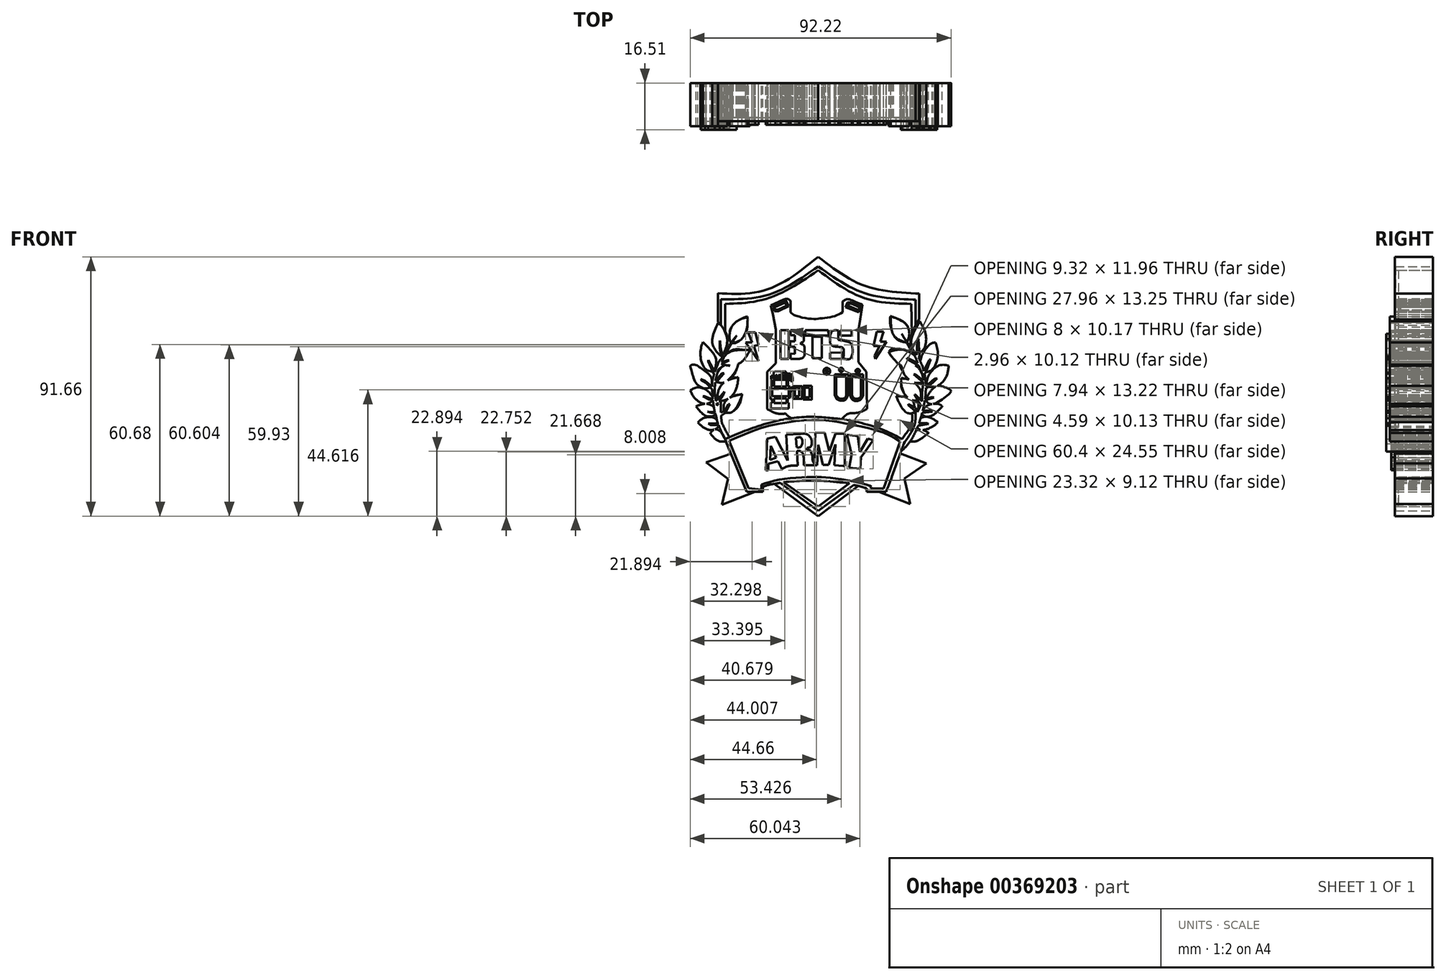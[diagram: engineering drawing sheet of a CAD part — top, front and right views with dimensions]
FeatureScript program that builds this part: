
annotation { "Feature Type Name" : "Feature", "Feature Type Description" : "" }
export const myFeature = defineFeature(function(context is Context, id is Id, definition is map)
    precondition{}
    {
        {
            var Q0;
            Q0=qCreatedBy(makeId("Front.planeOp"),FACE);
            var sketch = newSketch(context, id + "F0", { "sketchPlane" : qUnion([Q0])});
            skFitSpline(sketch, "E0", {"points": [v(-30.19, 8) * mm, v(-27.2, 9.29) * mm, v(-25.23, 13.15) * mm, v(-24.96, 17.16) * mm], "startDerivative": vector(10.5, 2.6) * mm, "endDerivative": vector(-0.16, 11.52) * mm});
            skFitSpline(sketch, "E1", {"points": [v(-24.96, 17.16) * mm, v(-28.56, 15.8) * mm, v(-31.07, 12.48) * mm, v(-31, 8.26) * mm, v(-30.19, 8) * mm], "startDerivative": vector(-13.43, -3.63) * mm, "endDerivative": vector(6.8, 0.18) * mm});
            skFitSpline(sketch, "E2", {"points": [v(-34.2, 3.24) * mm, v(-36.37, 5.48) * mm, v(-37.45, 9.08) * mm, v(-35.42, 15.06) * mm], "startDerivative": vector(-8.23, 7.14) * mm, "endDerivative": vector(7.27, 15.47) * mm});
            skFitSpline(sketch, "E3", {"points": [v(-34.2, 3.24) * mm, v(-32.9, 5.55) * mm, v(-32.23, 9.56) * mm, v(-34.2, 14.04) * mm, v(-35.42, 15.06) * mm], "startDerivative": vector(5.9, 9.32) * mm, "endDerivative": vector(-6.57, 4.06) * mm});
            skFitSpline(sketch, "E4", {"points": [v(-36.9, -2.26) * mm, v(-36.1, 0.6) * mm, v(-36.43, 3.24) * mm, v(-40.78, 8.26) * mm], "startDerivative": vector(3.44, 9.98) * mm, "endDerivative": vector(-12.5, 12.2) * mm});
            skFitSpline(sketch, "E5", {"points": [v(-36.9, -2.26) * mm, v(-39.56, -1.44) * mm, v(-41.4, 1.82) * mm, v(-41.46, 6.1) * mm, v(-40.78, 8.26) * mm], "startDerivative": vector(-12.2, 1.64) * mm, "endDerivative": vector(3.69, 9.25) * mm});
            skFitSpline(sketch, "E6", {"points": [v(-34.26, 0.6) * mm, v(-31.27, 0) * mm, v(-27.2, 1.2) * mm, v(-24.15, 5.48) * mm], "startDerivative": vector(9.82, -3) * mm, "endDerivative": vector(6.9, 13.15) * mm});
            skFitSpline(sketch, "E7", {"points": [v(-34.26, 0.6) * mm, v(-32.43, 4.06) * mm, v(-28.5, 5.48) * mm, v(-24.15, 5.48) * mm], "startDerivative": vector(4.12, 12.1) * mm, "endDerivative": vector(12.58, -0.7) * mm});
            skFitSpline(sketch, "E8", {"points": [v(-37.66, -7.35) * mm, v(-37.86, -4.09) * mm, v(-40.78, -1.44) * mm, v(-43.5, 0.3) * mm, v(-45.26, 0) * mm], "startDerivative": vector(1.6, 13.32) * mm, "endDerivative": vector(-8.96, -3.42) * mm});
            skFitSpline(sketch, "E9", {"points": [v(-37.66, -7.35) * mm, v(-39.56, -8.1) * mm, v(-42.82, -6.6) * mm, v(-44.68, -2.26) * mm, v(-45.26, 0) * mm], "startDerivative": vector(-8.4, -5.24) * mm, "endDerivative": vector(-2.34, 9.18) * mm});
            skFitSpline(sketch, "E10", {"points": [v(-36.4, -5.58) * mm, v(-33.33, -6) * mm, v(-29.37, -2.26) * mm, v(-28.26, 0.6) * mm], "startDerivative": vector(9.84, -3.85) * mm, "endDerivative": vector(2.3, 8.84) * mm});
            skFitSpline(sketch, "E11", {"points": [v(-36.4, -5.58) * mm, v(-35.4, -2.26) * mm, v(-33.33, 0.3) * mm], "startDerivative": vector(1.38, 6.92) * mm, "endDerivative": vector(4.77, 4.85) * mm});
            skFitSpline(sketch, "E12", {"points": [v(-35.4, -12.71) * mm, v(-35.4, -9.32) * mm, v(-33.27, -5.97) * mm, v(-28.26, -4.09) * mm], "startDerivative": vector(-1.3, 11.27) * mm, "endDerivative": vector(14.74, 3.55) * mm});
            skFitSpline(sketch, "E13", {"points": [v(-35.4, -12.71) * mm, v(-31.2, -11.35) * mm, v(-28.83, -7.7) * mm, v(-28.26, -4.09) * mm], "startDerivative": vector(13.25, 2.2) * mm, "endDerivative": vector(0.85, 11.32) * mm});
            skFitSpline(sketch, "E14", {"points": [v(-36.9, -12.03) * mm, v(-39.56, -13.53) * mm, v(-43.22, -11.96) * mm, v(-45.26, -8.77) * mm], "startDerivative": vector(-7.9, -6.9) * mm, "endDerivative": vector(-4.64, 9.96) * mm});
            skFitSpline(sketch, "E15", {"points": [v(-36.9, -12.03) * mm, v(-38.97, -9.05) * mm, v(-42.61, -7.7) * mm, v(-45.26, -8.77) * mm], "startDerivative": vector(-4.78, 9.51) * mm, "endDerivative": vector(-8.06, -5.02) * mm});
            skFitSpline(sketch, "E16", {"points": [v(-33.28, -16.41) * mm, v(-30.23, -16.27) * mm, v(-27.25, -11.35) * mm, v(-26.88, -10.09) * mm], "startDerivative": vector(9.47, -2.39) * mm, "endDerivative": vector(0.94, 4.4) * mm});
            skFitSpline(sketch, "E17", {"points": [v(-33.28, -16.41) * mm, v(-33.28, -13.5) * mm, v(-31.2, -11.35) * mm, v(-26.88, -10.09) * mm], "startDerivative": vector(-1.48, 9.93) * mm, "endDerivative": vector(12.19, 2.44) * mm});
            skFitSpline(sketch, "E18", {"points": [v(-35.38, -16.41) * mm, v(-36.91, -17.72) * mm, v(-39.82, -17.72) * mm, v(-43.23, -14.38) * mm], "startDerivative": vector(-4.87, -5.65) * mm, "endDerivative": vector(-7.8, 10.14) * mm});
            skFitSpline(sketch, "E19", {"points": [v(-35.38, -16.41) * mm, v(-37.06, -14.52) * mm, v(-39.56, -13.53) * mm, v(-43.23, -14.38) * mm], "startDerivative": vector(-4.92, 6.62) * mm, "endDerivative": vector(-10.15, -3.6) * mm});
            skFitSpline(sketch, "E20", {"points": [v(-34.66, -20.92) * mm, v(-36.47, -22.51) * mm, v(-39.56, -22.44) * mm, v(-42.5, -20.12) * mm], "startDerivative": vector(-5.28, -6.44) * mm, "endDerivative": vector(-7.41, 7.58) * mm});
            skFitSpline(sketch, "E21", {"points": [v(-34.66, -20.92) * mm, v(-36.62, -18.6) * mm, v(-40.18, -18.45) * mm, v(-42.5, -20.12) * mm], "startDerivative": vector(-4.76, 8.44) * mm, "endDerivative": vector(-6.36, -6.26) * mm});
            skFitSpline(sketch, "E22", {"points": [v(-32.55, -26.73) * mm, v(-35.18, -26.73) * mm, v(-38.22, -23.9) * mm], "startDerivative": vector(-6.04, -1.13) * mm, "endDerivative": vector(-5.32, 6.5) * mm});
            skFitSpline(sketch, "E23", {"points": [v(-32.55, -26.73) * mm, v(-34.08, -23.97) * mm, v(-34.66, -23.1) * mm], "startDerivative": vector(-2.66, 4.98) * mm, "endDerivative": vector(-1.44, 2.03) * mm});
            skFitSpline(sketch, "E24", {"points": [v(-34.48, -23.34) * mm, v(-36.47, -22.51) * mm, v(-38.16, -23.97) * mm], "startDerivative": vector(-4.18, 2.8) * mm, "endDerivative": vector(-3.17, -4.03) * mm});
            skFitSpline(sketch, "E25", {"points": [v(31.17, 8.2) * mm, v(28.13, 9.37) * mm, v(26.18, 11.82) * mm, v(25.69, 17.4) * mm], "startDerivative": vector(-10.62, 3.25) * mm, "endDerivative": vector(0.13, 15.42) * mm});
            skFitSpline(sketch, "E26", {"points": [v(31.17, 8.2) * mm, v(32.15, 10.35) * mm, v(31.17, 14.46) * mm, v(25.69, 17.4) * mm], "startDerivative": vector(4.76, 7.94) * mm, "endDerivative": vector(-15.88, 5.4) * mm});
            skFitSpline(sketch, "E27", {"points": [v(34.79, 3.6) * mm, v(37.62, 6.44) * mm, v(37.92, 11.33) * mm, v(35.96, 15.63) * mm], "startDerivative": vector(10.72, 7.67) * mm, "endDerivative": vector(-6.93, 11.9) * mm});
            skFitSpline(sketch, "E28", {"points": [v(34.79, 3.6) * mm, v(32.83, 8.2) * mm, v(35.96, 15.63) * mm], "startDerivative": vector(-6.65, 9.81) * mm, "endDerivative": vector(8.4, 14.08) * mm});
            skFitSpline(sketch, "E29", {"points": [v(34.79, 0) * mm, v(32.15, 0) * mm, v(29.4, 0) * mm, v(25.69, 3.6) * mm, v(24.7, 5.36) * mm], "startDerivative": vector(-11.4, 0.72) * mm, "endDerivative": vector(-3.42, 7.43) * mm});
            skFitSpline(sketch, "E30", {"points": [v(34.79, 0) * mm, v(34.79, 2.62) * mm, v(31.17, 5.26) * mm, v(28.23, 5.66) * mm, v(24.94, 4.86) * mm], "startDerivative": vector(2.96, 12.02) * mm, "endDerivative": vector(-13.45, -4.04) * mm});
            skFitSpline(sketch, "E31", {"points": [v(37.43, -2.46) * mm, v(40.27, -1.39) * mm, v(42.32, 3.6) * mm, v(41.44, 8.2) * mm], "startDerivative": vector(10.74, 1.63) * mm, "endDerivative": vector(-4.28, 12.5) * mm});
            skFitSpline(sketch, "E32", {"points": [v(37.43, -2.46) * mm, v(35.96, 0.96) * mm, v(39.29, 7.32) * mm, v(41.44, 8.2) * mm], "startDerivative": vector(-7.42, 9.22) * mm, "endDerivative": vector(8.15, 1.13) * mm});
            skFitSpline(sketch, "E33", {"points": [v(38.3, -7.45) * mm, v(41.44, -7.45) * mm, v(45.06, -4.32) * mm, v(46.14, 0) * mm], "startDerivative": vector(10.39, 0.61) * mm, "endDerivative": vector(1.3, 12.96) * mm});
            skFitSpline(sketch, "E34", {"points": [v(38.3, -7.45) * mm, v(39, -3.64) * mm, v(42.61, 0) * mm, v(46.14, 0) * mm], "startDerivative": vector(0.09, 13.1) * mm, "endDerivative": vector(11.66, -2.26) * mm});
            skFitSpline(sketch, "E35", {"points": [v(38.3, -12.25) * mm, v(40.27, -13.62) * mm, v(45.25, -10.88) * mm, v(46.93, -8.82) * mm, v(44.18, -7.45) * mm, v(41.44, -7.45) * mm, v(38.3, -12.25) * mm]});
            skFitSpline(sketch, "E36", {"points": [v(36.16, -16.65) * mm, v(37.92, -18.02) * mm, v(40.36, -17.63) * mm, v(43.89, -14.4) * mm], "startDerivative": vector(5.7, -6.05) * mm, "endDerivative": vector(8.4, 9.26) * mm});
            skFitSpline(sketch, "E37", {"points": [v(36.16, -16.65) * mm, v(38.3, -14.3) * mm, v(40.27, -13.62) * mm, v(42.61, -13.62) * mm, v(43.89, -14.4) * mm], "startDerivative": vector(7.08, 9.2) * mm, "endDerivative": vector(5.46, -4.64) * mm});
            skFitSpline(sketch, "E38", {"points": [v(36.16, -12.25) * mm, v(33.32, -12.25) * mm, v(30.48, -10) * mm, v(29.3, -6.08) * mm, v(29.3, -4.52) * mm], "startDerivative": vector(-11.56, -1.6) * mm, "endDerivative": vector(0.5, 7.43) * mm});
            skFitSpline(sketch, "E39", {"points": [v(36.16, -12.25) * mm, v(36.16, -8.92) * mm, v(33.12, -5.4) * mm, v(29.3, -4.52) * mm], "startDerivative": vector(1.87, 10.7) * mm, "endDerivative": vector(-11.7, 0.9) * mm});
            skFitSpline(sketch, "E40", {"points": [v(34, -16.65) * mm, v(31.26, -16.65) * mm, v(28.13, -12.25) * mm, v(27.45, -10.2) * mm], "startDerivative": vector(-9.07, -2.55) * mm, "endDerivative": vector(-1.62, 6.4) * mm});
            skFitSpline(sketch, "E41", {"points": [v(34, -16.65) * mm, v(34, -14.4) * mm, v(33.32, -12.25) * mm, v(31.56, -11.28) * mm, v(27.6, -10.77) * mm], "startDerivative": vector(0.5, 9.44) * mm, "endDerivative": vector(-13.88, 1.15) * mm});
            skFitSpline(sketch, "E42", {"points": [v(34.66, -21.04) * mm, v(36.17, -22.78) * mm, v(40.46, -21.54) * mm, v(42.28, -20.04) * mm], "startDerivative": vector(3.62, -7.81) * mm, "endDerivative": vector(4.77, 4.93) * mm});
            skFitSpline(sketch, "E43", {"points": [v(34.66, -21.04) * mm, v(35.62, -19.03) * mm, v(38.5, -18.13) * mm, v(42.28, -20.04) * mm], "startDerivative": vector(2.13, 7.76) * mm, "endDerivative": vector(9.59, -6.77) * mm});
            skFitSpline(sketch, "E44", {"points": [v(32.29, -26.75) * mm, v(33.66, -24.74) * mm, v(34.66, -22.82) * mm], "startDerivative": vector(2.81, 3.9) * mm, "endDerivative": vector(1.92, 3.96) * mm});
            skFitSpline(sketch, "E45", {"points": [v(32.29, -26.75) * mm, v(34.66, -26.75) * mm, v(39.04, -23.78) * mm], "startDerivative": vector(5.64, -1) * mm, "endDerivative": vector(7.73, 6.44) * mm});
            skFitSpline(sketch, "E46", {"points": [v(34.66, -22.82) * mm, v(37, -22.82) * mm, v(39.04, -23.78) * mm], "startDerivative": vector(4.77, 0.49) * mm, "endDerivative": vector(4, -2.41) * mm});
            skFitSpline(sketch, "E47", {"points": [v(-33.33, 0.3) * mm, v(-31.27, 0) * mm, v(-28.26, 0.6) * mm], "startDerivative": vector(4.34, -1.08) * mm, "endDerivative": vector(5.76, 1.57) * mm});
            skFitSpline(sketch, "E48", {"points": [v(36.92, -6.05) * mm, v(34.07, -6.05) * mm, v(30.8, -3.64) * mm, v(29.4, 0) * mm], "startDerivative": vector(-9.37, -1.43) * mm, "endDerivative": vector(-2.65, 10.96) * mm});
            skFitSpline(sketch, "E49", {"points": [v(36.92, -6.05) * mm, v(36.92, -3.64) * mm, v(34.34, 0.03) * mm, v(29.4, 0) * mm], "startDerivative": vector(1.31, 8.33) * mm, "endDerivative": vector(-14.13, -2.96) * mm});
            skSolve(sketch);
        }
        {
            var Q0;
            Q0=qCreatedBy(makeId("Front.planeOp"),FACE);
            var sketch = newSketch(context, id + "F1", { "sketchPlane" : qUnion([Q0])});
            skFitSpline(sketch, "E50", {"points": [v(-35.48, 25.53) * mm, v(-17.96, 26.92) * mm, v(0, 38.42) * mm], "startDerivative": vector(37.43, -1.62) * mm, "endDerivative": vector(33.59, 26.94) * mm});
            skFitSpline(sketch, "E51", {"points": [v(0, 38.42) * mm, v(16.05, 28.37) * mm, v(34.4, 25.5) * mm], "startDerivative": vector(30.7, -23.57) * mm, "endDerivative": vector(38.12, -2.26) * mm});
            skLineSegment(sketch, "E52", {"start": v(-35.48, 25.53) * mm, "end": v(-35.48, 15.4) * mm});
            skLineSegment(sketch, "E53", {"start": v(-35.48, 15.4) * mm, "end": v(-34.38, 14.35) * mm});
            skLineSegment(sketch, "E54", {"start": v(-34.38, 14.35) * mm, "end": v(-34.38, 23.46) * mm});
            skFitSpline(sketch, "E55", {"points": [v(-34.38, 23.46) * mm, v(-17.39, 25.15) * mm, v(0, 35.04) * mm], "startDerivative": vector(35.88, -0.2) * mm, "endDerivative": vector(32.95, 23.07) * mm});
            skFitSpline(sketch, "E56", {"points": [v(0, 35.04) * mm, v(16.05, 25.74) * mm, v(33.52, 23.3) * mm], "startDerivative": vector(30.76, -21.78) * mm, "endDerivative": vector(36.3, -1.62) * mm});
            skLineSegment(sketch, "E57", {"start": v(34.4, 25.5) * mm, "end": v(35.72, 25.5) * mm});
            skLineSegment(sketch, "E58", {"start": v(35.72, 25.5) * mm, "end": v(35.72, 16.36) * mm});
            skLineSegment(sketch, "E59", {"start": v(35.72, 16.36) * mm, "end": v(34.4, 14.33) * mm});
            skLineSegment(sketch, "E60", {"start": v(34.4, 14.33) * mm, "end": v(34.4, 23.3) * mm});
            skLineSegment(sketch, "E61", {"start": v(34.4, 23.3) * mm, "end": v(33.52, 23.3) * mm});
            skLineSegment(sketch, "E62", {"start": v(-34.38, 14.35) * mm, "end": v(-34.38, 14.33) * mm});
            skLineSegment(sketch, "E63", {"start": v(-32.88, 21.84) * mm, "end": v(-32.88, 12.15) * mm});
            skLineSegment(sketch, "E64", {"start": v(-32.88, 12.15) * mm, "end": v(-34.38, 14.33) * mm});
            skLineSegment(sketch, "E65", {"start": v(34.4, 14.33) * mm, "end": v(33.13, 10.98) * mm});
            skFitSpline(sketch, "E66", {"points": [v(-32.88, 21.84) * mm, v(-17.25, 23.97) * mm, v(0, 33.72) * mm], "startDerivative": vector(33.29, 0.5) * mm, "endDerivative": vector(32.48, 22.28) * mm});
            skFitSpline(sketch, "E67", {"points": [v(0, 33.72) * mm, v(16.05, 23.97) * mm, v(32.92, 21.84) * mm], "startDerivative": vector(30.35, -22.74) * mm, "endDerivative": vector(34.37, -0.2) * mm});
            skLineSegment(sketch, "E68", {"start": v(32.92, 21.84) * mm, "end": v(33.13, 10.98) * mm});
            skLineSegment(sketch, "E69", {"start": v(-35.48, 25.53) * mm, "end": v(-32.84, 26.82) * mm});
            skFitSpline(sketch, "E70", {"points": [v(-32.84, 26.82) * mm, v(-17.96, 28.82) * mm, v(0, 38.42) * mm], "startDerivative": vector(31.94, 1.22) * mm, "endDerivative": vector(33.7, 21.47) * mm});
            skLineSegment(sketch, "E71", {"start": v(35.72, 25.5) * mm, "end": v(32.96, 27.12) * mm});
            skFitSpline(sketch, "E72", {"points": [v(32.96, 27.12) * mm, v(16.05, 29.83) * mm, v(0, 38.42) * mm], "startDerivative": vector(-35.02, 2.69) * mm, "endDerivative": vector(-30.92, 19.82) * mm});
            skFitSpline(sketch, "E73", {"points": [v(-32.88, 12.15) * mm, v(-32.05, 9.37) * mm, v(-32.88, 4.8) * mm], "startDerivative": vector(2.6, -5.84) * mm, "endDerivative": vector(-2.42, -8.3) * mm});
            skFitSpline(sketch, "E74", {"points": [v(-35.48, 15.4) * mm, v(-36.95, 12.15) * mm, v(-37.32, 8.02) * mm, v(-35.97, 4.59) * mm, v(-34.09, 2.66) * mm], "startDerivative": vector(-6.38, -11.95) * mm, "endDerivative": vector(6.56, -7.11) * mm});
            skFitSpline(sketch, "E75", {"points": [v(-34.75, 8.82) * mm, v(-34.75, 5.87) * mm, v(-33.86, 3.18) * mm], "startDerivative": vector(-0.51, -5.9) * mm, "endDerivative": vector(2.47, -4.8) * mm});
            skFitSpline(sketch, "E76", {"points": [v(-33.44, 3.88) * mm, v(-33.95, 4.57) * mm, v(-34.39, 5.87) * mm, v(-34.75, 8.82) * mm], "startDerivative": vector(-1.94, 2.54) * mm, "endDerivative": vector(-0.63, 7.04) * mm});
            skFitSpline(sketch, "E77", {"points": [v(-30.85, 8) * mm, v(-31.29, 11.2) * mm, v(-30.57, 13.69) * mm, v(-26.06, 17.04) * mm, v(-24.97, 17.3) * mm], "startDerivative": vector(-1.4, 12.48) * mm, "endDerivative": vector(5.47, 0.32) * mm});
            skFitSpline(sketch, "E78", {"points": [v(-30.53, 8) * mm, v(-29.15, 8) * mm, v(-26.31, 10.31) * mm, v(-25.13, 13.15) * mm, v(-24.97, 17.3) * mm], "startDerivative": vector(8.6, -1.68) * mm, "endDerivative": vector(-0.22, 15.04) * mm});
            skFitSpline(sketch, "E79", {"points": [v(-34.32, 0.69) * mm, v(-31.47, -0.37) * mm, v(-26.55, 1.82) * mm, v(-24.4, 5.17) * mm], "startDerivative": vector(8.72, -5.5) * mm, "endDerivative": vector(4.72, 10.6) * mm});
            skFitSpline(sketch, "E80", {"points": [v(-32.61, 3.95) * mm, v(-29.8, 5.64) * mm, v(-24.4, 5.17) * mm], "startDerivative": vector(5.74, 4.88) * mm, "endDerivative": vector(10.48, -2.16) * mm});
            skFitSpline(sketch, "E81", {"points": [v(-36.38, -5.86) * mm, v(-33.3, -6.06) * mm, v(-29.76, -3.25) * mm, v(-28.31, 0.59) * mm], "startDerivative": vector(9.85, -3.58) * mm, "endDerivative": vector(2.78, 11.3) * mm});
            skFitSpline(sketch, "E82", {"points": [v(-35.26, -1.35) * mm, v(-34.17, -0.51) * mm, v(-33.1, 0) * mm], "startDerivative": vector(1.95, 1.82) * mm, "endDerivative": vector(2.24, 0.92) * mm});
            skFitSpline(sketch, "E83", {"points": [v(-37.2, -2.17) * mm, v(-39.89, -1.24) * mm, v(-41.43, 2) * mm, v(-41.23, 7.88) * mm, v(-40.92, 8.55) * mm], "startDerivative": vector(-11.92, 2.33) * mm, "endDerivative": vector(2.54, 3.57) * mm});
            skFitSpline(sketch, "E84", {"points": [v(-35.96, -0.73) * mm, v(-36.02, 3.03) * mm, v(-40.92, 8.55) * mm], "startDerivative": vector(1.42, 9) * mm, "endDerivative": vector(-10.77, 9.58) * mm});
            skFitSpline(sketch, "E85", {"points": [v(-38.28, -7.54) * mm, v(-40.92, -7.63) * mm, v(-44.73, -3.25) * mm, v(-45.6, 0) * mm], "startDerivative": vector(-8.99, -2.33) * mm, "endDerivative": vector(-0.88, 9.59) * mm});
            skFitSpline(sketch, "E86", {"points": [v(-37.93, -7.01) * mm, v(-38.24, -3.92) * mm, v(-41.43, -0.73) * mm, v(-45.6, 0) * mm], "startDerivative": vector(0.72, 10.17) * mm, "endDerivative": vector(-11.2, 0.59) * mm});
            skFitSpline(sketch, "E87", {"points": [v(-35.04, -12.58) * mm, v(-32.36, -12.37) * mm, v(-29.69, -9.38) * mm, v(-28.76, -5.86) * mm, v(-28.8, -4.28) * mm], "startDerivative": vector(11.3, -1.17) * mm, "endDerivative": vector(-0.76, 7.7) * mm});
            skFitSpline(sketch, "E88", {"points": [v(-28.8, -4.28) * mm, v(-30.05, -4.28) * mm, v(-31.09, -4.76) * mm], "startDerivative": vector(-2.49, 0.26) * mm, "endDerivative": vector(-1.87, -1.22) * mm});
            skFitSpline(sketch, "E89", {"points": [v(-32.73, -16.65) * mm, v(-30.2, -16.18) * mm, v(-27.83, -13.6) * mm, v(-27.1, -10.41) * mm], "startDerivative": vector(8.44, 0.24) * mm, "endDerivative": vector(1.01, 9.46) * mm});
            skFitSpline(sketch, "E90", {"points": [v(-33.42, -16.24) * mm, v(-33.24, -13.71) * mm, v(-32.36, -12.37) * mm], "startDerivative": vector(-0.06, 3.41) * mm, "endDerivative": vector(2.13, 2.56) * mm});
            skFitSpline(sketch, "E91", {"points": [v(-30.68, -10.97) * mm, v(-28.8, -10.41) * mm, v(-27.1, -10.41) * mm], "startDerivative": vector(3.65, 1.34) * mm, "endDerivative": vector(3.5, -0.26) * mm});
            skFitSpline(sketch, "E92", {"points": [v(-37.19, -12.58) * mm, v(-39.8, -13.5) * mm, v(-43.08, -12.37) * mm, v(-45.92, -8.83) * mm], "startDerivative": vector(-8.47, -4.4) * mm, "endDerivative": vector(-6.77, 10.62) * mm});
            skFitSpline(sketch, "E93", {"points": [v(-37.37, -10.41) * mm, v(-39.87, -8.54) * mm, v(-42.79, -7.75) * mm, v(-45.92, -8.83) * mm], "startDerivative": vector(-7.16, 6.25) * mm, "endDerivative": vector(-9.16, -4.01) * mm});
            skFitSpline(sketch, "E94", {"points": [v(-36.11, -17.76) * mm, v(-38.49, -18.33) * mm, v(-42.28, -16.04) * mm, v(-43.08, -14.66) * mm], "startDerivative": vector(-6.75, -3.48) * mm, "endDerivative": vector(-1.86, 4.98) * mm});
            skFitSpline(sketch, "E95", {"points": [v(-40.84, -13.41) * mm, v(-43.08, -14.66) * mm], "startDerivative": vector(-2.24, -1.23) * mm, "endDerivative": vector(-2.24, -1.23) * mm});
            skFitSpline(sketch, "E96", {"points": [v(-36.94, -14.42) * mm, v(-38.05, -13.86) * mm, v(-39.8, -13.5) * mm], "startDerivative": vector(-2.27, 1.36) * mm, "endDerivative": vector(-3.42, 0.52) * mm});
            skFitSpline(sketch, "E97", {"points": [v(-35, -21.58) * mm, v(-36.37, -22.66) * mm, v(-38.95, -22.6) * mm, v(-42.53, -20.15) * mm], "startDerivative": vector(-4.62, -4.85) * mm, "endDerivative": vector(-8.56, 7.26) * mm});
            skFitSpline(sketch, "E98", {"points": [v(-35.78, -19.44) * mm, v(-36.92, -18.59) * mm, v(-38.22, -18.37) * mm, v(-40.27, -18.67) * mm, v(-42.53, -20.15) * mm], "startDerivative": vector(-5.1, 4.54) * mm, "endDerivative": vector(-7.26, -5.81) * mm});
            skFitSpline(sketch, "E99", {"points": [v(-32.58, -26.84) * mm, v(-34.53, -26.75) * mm, v(-38.2, -24.09) * mm], "startDerivative": vector(-4.7, -0.61) * mm, "endDerivative": vector(-6.41, 5.68) * mm});
            skFitSpline(sketch, "E100", {"points": [v(-34.53, -22.65) * mm, v(-35.85, -22.6) * mm, v(-38.2, -24.09) * mm], "startDerivative": vector(-3.11, 0.67) * mm, "endDerivative": vector(-4.17, -3.32) * mm});
            skLineSegment(sketch, "E101", {"start": v(-36.82, -3.15) * mm, "end": v(-38.92, 1.5) * mm});
            skLineSegment(sketch, "E102", {"start": v(-38.92, 1.5) * mm, "end": v(-38.92, 1.97) * mm});
            skLineSegment(sketch, "E103", {"start": v(-38.92, 1.97) * mm, "end": v(-36.52, -2.17) * mm});
            skLineSegment(sketch, "E104", {"start": v(-34.18, 0.6) * mm, "end": v(-31.48, 1.87) * mm});
            skLineSegment(sketch, "E105", {"start": v(-31.48, 1.87) * mm, "end": v(-32.17, 1.87) * mm});
            skLineSegment(sketch, "E106", {"start": v(-32.17, 1.87) * mm, "end": v(-34.02, 1.27) * mm});
            skLineSegment(sketch, "E107", {"start": v(-36.03, -5.98) * mm, "end": v(-34.52, -4.15) * mm});
            skLineSegment(sketch, "E108", {"start": v(-34.52, -4.15) * mm, "end": v(-33.3, -2.73) * mm});
            skLineSegment(sketch, "E109", {"start": v(-33.3, -2.73) * mm, "end": v(-34.08, -2.73) * mm});
            skLineSegment(sketch, "E110", {"start": v(-34.08, -2.73) * mm, "end": v(-36.21, -5.21) * mm});
            skLineSegment(sketch, "E111", {"start": v(-36.21, -5.21) * mm, "end": v(-36.32, -5.31) * mm});
            skLineSegment(sketch, "E112", {"start": v(-37.41, -7.44) * mm, "end": v(-37.93, -7.01) * mm});
            skLineSegment(sketch, "E113", {"start": v(-37.93, -7.01) * mm, "end": v(-39.97, -5.4) * mm});
            skLineSegment(sketch, "E114", {"start": v(-39.97, -5.4) * mm, "end": v(-41.5, -4.75) * mm});
            skLineSegment(sketch, "E115", {"start": v(-41.5, -4.75) * mm, "end": v(-41.31, -5.08) * mm});
            skLineSegment(sketch, "E116", {"start": v(-41.31, -5.08) * mm, "end": v(-39.79, -5.98) * mm});
            skLineSegment(sketch, "E117", {"start": v(-39.79, -5.98) * mm, "end": v(-37.43, -8.42) * mm});
            skLineSegment(sketch, "E118", {"start": v(-35.95, -13.4) * mm, "end": v(-35.04, -12.58) * mm});
            skLineSegment(sketch, "E119", {"start": v(-35.04, -12.58) * mm, "end": v(-33.63, -10.62) * mm});
            skLineSegment(sketch, "E120", {"start": v(-33.63, -10.62) * mm, "end": v(-33.09, -9.2) * mm});
            skLineSegment(sketch, "E121", {"start": v(-33.09, -9.2) * mm, "end": v(-33.2, -9.5) * mm});
            skPoint(sketch, "E122.1.internal.snap0", {"position": v(-35.28, -5.07) * mm});
            skFitSpline(sketch, "E122", {"points": [v(-36.1, -12.48) * mm, v(-35.28, -11.6) * mm, v(-33.09, -9.2) * mm], "startDerivative": vector(1.91, 2.04) * mm, "endDerivative": vector(3.94, 4.34) * mm});
            skLineSegment(sketch, "E123", {"start": v(-37.21, -12.3) * mm, "end": v(-38.64, -12.01) * mm});
            skLineSegment(sketch, "E124", {"start": v(-38.64, -12.01) * mm, "end": v(-40.81, -10.87) * mm});
            skLineSegment(sketch, "E125", {"start": v(-40.81, -10.87) * mm, "end": v(-40.16, -10.87) * mm});
            skLineSegment(sketch, "E126", {"start": v(-40.16, -10.87) * mm, "end": v(-38.64, -11.54) * mm});
            skLineSegment(sketch, "E127", {"start": v(-38.64, -11.54) * mm, "end": v(-37.26, -11.82) * mm});
            skLineSegment(sketch, "E128", {"start": v(-34.47, -12.63) * mm, "end": v(-34.47, -16.62) * mm});
            skLineSegment(sketch, "E129", {"start": v(-35.82, -14.1) * mm, "end": v(-35.13, -13.38) * mm});
            skLineSegment(sketch, "E130", {"start": v(-35.13, -13.38) * mm, "end": v(-35.95, -13.4) * mm});
            skLineSegment(sketch, "E131", {"start": v(-21.07, 1.63) * mm, "end": v(-25.66, 8.18) * mm});
            skLineSegment(sketch, "E132", {"start": v(-25.66, 8.18) * mm, "end": v(-23.4, 8.18) * mm});
            skLineSegment(sketch, "E133", {"start": v(-23.4, 8.18) * mm, "end": v(-24.71, 11.75) * mm});
            skLineSegment(sketch, "E134", {"start": v(-24.71, 11.75) * mm, "end": v(-22.24, 11.75) * mm});
            skLineSegment(sketch, "E135", {"start": v(-22.24, 11.75) * mm, "end": v(-21.07, 7.3) * mm});
            skLineSegment(sketch, "E136", {"start": v(-21.07, 7.3) * mm, "end": v(-22.77, 6.86) * mm});
            skLineSegment(sketch, "E137", {"start": v(-22.77, 6.86) * mm, "end": v(-21.07, 1.63) * mm});
            skLineSegment(sketch, "E138", {"start": v(-33.97, -20.44) * mm, "end": v(-34.28, -18.46) * mm});
            skLineSegment(sketch, "E139", {"start": v(-34.28, -18.46) * mm, "end": v(-34.28, -17.76) * mm});
            skLineSegment(sketch, "E140", {"start": v(-34.28, -17.76) * mm, "end": v(-32.73, -16.65) * mm});
            skLineSegment(sketch, "E141", {"start": v(-32.73, -16.65) * mm, "end": v(-31.24, -13.68) * mm});
            skLineSegment(sketch, "E142", {"start": v(-31.24, -13.68) * mm, "end": v(-31.7, -13.68) * mm});
            skLineSegment(sketch, "E143", {"start": v(-31.7, -13.68) * mm, "end": v(-33.02, -16.1) * mm});
            skLineSegment(sketch, "E144", {"start": v(-33.02, -16.1) * mm, "end": v(-34.47, -16.62) * mm});
            skLineSegment(sketch, "E145", {"start": v(-36.5, -16.73) * mm, "end": v(-37.75, -16.73) * mm});
            skLineSegment(sketch, "E146", {"start": v(-37.75, -16.73) * mm, "end": v(-39.07, -16.27) * mm});
            skLineSegment(sketch, "E147", {"start": v(-39.07, -16.27) * mm, "end": v(-38.8, -16.27) * mm});
            skLineSegment(sketch, "E148", {"start": v(-38.8, -16.27) * mm, "end": v(-37.7, -16.48) * mm});
            skLineSegment(sketch, "E149", {"start": v(-37.7, -16.48) * mm, "end": v(-36.56, -16.48) * mm});
            skLineSegment(sketch, "E150", {"start": v(-35.39, -20.57) * mm, "end": v(-38.8, -20.57) * mm});
            skLineSegment(sketch, "E151", {"start": v(-38.8, -20.57) * mm, "end": v(-38.02, -20.95) * mm});
            skLineSegment(sketch, "E152", {"start": v(-38.02, -20.95) * mm, "end": v(-35.25, -20.95) * mm});
            skLineSegment(sketch, "E153", {"start": v(-35.2, -8.41) * mm, "end": v(-35.4, -6.22) * mm});
            skLineSegment(sketch, "E154", {"start": v(-32.88, -26) * mm, "end": v(-32.58, -26.84) * mm});
            skLineSegment(sketch, "E155", {"start": v(-32.58, -26.84) * mm, "end": v(-25.27, -44.62) * mm});
            skLineSegment(sketch, "E156", {"start": v(-25.27, -44.62) * mm, "end": v(-19.5, -44.62) * mm});
            skLineSegment(sketch, "E157", {"start": v(-30.82, -31.12) * mm, "end": v(-39.6, -34.26) * mm});
            skLineSegment(sketch, "E158", {"start": v(-39.6, -34.26) * mm, "end": v(-31.92, -40.03) * mm});
            skLineSegment(sketch, "E159", {"start": v(-31.92, -40.03) * mm, "end": v(-34.03, -49.15) * mm});
            skLineSegment(sketch, "E160", {"start": v(-34.03, -49.15) * mm, "end": v(-22.38, -44.62) * mm});
            skLineSegment(sketch, "E161", {"start": v(-31.45, -26.64) * mm, "end": v(-24.65, -43.38) * mm});
            skLineSegment(sketch, "E162", {"start": v(-24.65, -43.38) * mm, "end": v(-20.06, -43.85) * mm});
            skLineSegment(sketch, "E163", {"start": v(-20.06, -43.85) * mm, "end": v(-20.06, -42.04) * mm});
            skFitSpline(sketch, "E164", {"points": [v(-32.88, -26) * mm, v(-19.62, -20.9) * mm, v(-5.81, -18.22) * mm, v(3.57, -18.43) * mm, v(11.91, -19.56) * mm, v(22.84, -22.65) * mm, v(29.54, -26) * mm], "startDerivative": vector(67.2, 28.81) * mm, "endDerivative": vector(43.65, -24.82) * mm});
            skFitSpline(sketch, "E165", {"points": [v(-31.45, -26.64) * mm, v(-19.62, -21.93) * mm, v(-5.81, -19.46) * mm, v(3.57, -19.46) * mm, v(11.91, -20.9) * mm, v(22.73, -23.58) * mm, v(28.95, -26.84) * mm], "startDerivative": vector(61.23, 27.95) * mm, "endDerivative": vector(40.56, -25.42) * mm});
            skLineSegment(sketch, "E166", {"start": v(28.95, -26.84) * mm, "end": v(23.12, -43.55) * mm});
            skLineSegment(sketch, "E167", {"start": v(23.12, -43.55) * mm, "end": v(18.56, -43.55) * mm});
            skLineSegment(sketch, "E168", {"start": v(18.56, -43.55) * mm, "end": v(18.85, -42.82) * mm});
            skFitSpline(sketch, "E169", {"points": [v(-24.65, -43.38) * mm, v(-20.06, -42.04) * mm, v(-12.26, -40.12) * mm, v(-1.65, -39.4) * mm, v(6, -39.88) * mm, v(16.89, -42.04) * mm, v(18.85, -42.82) * mm], "startDerivative": vector(31.5, 8.99) * mm, "endDerivative": vector(15.84, -7.52) * mm});
            skLineSegment(sketch, "E170", {"start": v(-19.5, -42.82) * mm, "end": v(-19.5, -44.62) * mm});
            skLineSegment(sketch, "E171", {"start": v(23.95, -44.62) * mm, "end": v(17.1, -44.62) * mm});
            skLineSegment(sketch, "E172", {"start": v(17.1, -44.62) * mm, "end": v(17.1, -43.38) * mm});
            skFitSpline(sketch, "E173", {"points": [v(23.95, -44.62) * mm, v(25.78, -40.05) * mm, v(28.98, -31.08) * mm, v(30.26, -27.56) * mm], "startDerivative": vector(5.33, 12.92) * mm, "endDerivative": vector(3.31, 11.18) * mm});
            skFitSpline(sketch, "E174", {"points": [v(30.26, -27.56) * mm, v(33.18, -23.04) * mm, v(34.34, -19.55) * mm, v(34.34, -16.05) * mm], "startDerivative": vector(8.56, 12.15) * mm, "endDerivative": vector(-0.74, 11.55) * mm});
            skFitSpline(sketch, "E175", {"points": [v(29.54, -26) * mm, v(31.75, -23) * mm, v(33.2, -19.5) * mm, v(33.14, -16.58) * mm], "startDerivative": vector(6.68, 8.31) * mm, "endDerivative": vector(-1.2, 9.33) * mm});
            skLineSegment(sketch, "E176", {"start": v(21.48, -44.62) * mm, "end": v(32.48, -49.01) * mm});
            skLineSegment(sketch, "E177", {"start": v(32.48, -49.01) * mm, "end": v(30.51, -39.9) * mm});
            skLineSegment(sketch, "E178", {"start": v(30.51, -39.9) * mm, "end": v(38.24, -34.58) * mm});
            skLineSegment(sketch, "E179", {"start": v(38.24, -34.58) * mm, "end": v(28.98, -31.08) * mm});
            skLineSegment(sketch, "E180", {"start": v(-15.48, -41.82) * mm, "end": v(0, -53.24) * mm});
            skLineSegment(sketch, "E181", {"start": v(0, -53.24) * mm, "end": v(14.13, -42.55) * mm});
            skLineSegment(sketch, "E182", {"start": v(-13.44, -41.45) * mm, "end": v(0, -51.42) * mm});
            skLineSegment(sketch, "E183", {"start": v(0, -51.42) * mm, "end": v(12.56, -42.23) * mm});
            skLineSegment(sketch, "E184", {"start": v(-12.26, -41.21) * mm, "end": v(0, -49.8) * mm});
            skLineSegment(sketch, "E185", {"start": v(0, -49.8) * mm, "end": v(11.06, -41.65) * mm});
            skFitSpline(sketch, "E186", {"points": [v(-19.5, -42.82) * mm, v(-17.3, -42.12) * mm, v(-15.48, -41.82) * mm, v(-13.44, -41.45) * mm], "startDerivative": vector(6.42, 2.26) * mm, "endDerivative": vector(6.24, 1.23) * mm});
            skFitSpline(sketch, "E187", {"points": [v(-12.26, -41.21) * mm, v(-5.56, -40.74) * mm, v(1.54, -40.78) * mm, v(11.06, -41.65) * mm], "startDerivative": vector(21.62, 1.82) * mm, "endDerivative": vector(26.64, -2.87) * mm});
            skFitSpline(sketch, "E188", {"points": [v(12.56, -42.23) * mm, v(14.13, -42.55) * mm, v(17.1, -43.38) * mm], "startDerivative": vector(3.46, -0.62) * mm, "endDerivative": vector(5.52, -1.62) * mm});
            skLineSegment(sketch, "E189", {"start": v(-17.64, -36.97) * mm, "end": v(-18.56, -36.97) * mm});
            skLineSegment(sketch, "E190", {"start": v(-18.56, -36.97) * mm, "end": v(-18, -25.84) * mm});
            skLineSegment(sketch, "E191", {"start": v(-18, -25.84) * mm, "end": v(-15.17, -25.22) * mm});
            skLineSegment(sketch, "E192", {"start": v(-15.17, -25.22) * mm, "end": v(-10.84, -33.62) * mm});
            skFitSpline(sketch, "E193", {"points": [v(35.46, -16.63) * mm, v(35.46, -13.21) * mm], "startDerivative": vector(0, 3.08) * mm, "endDerivative": vector(0, 3.08) * mm});
            skFitSpline(sketch, "E194", {"points": [v(34.42, -14.9) * mm, v(32.48, -12.22) * mm, v(27.6, -10.13) * mm], "startDerivative": vector(-4.4, 6.07) * mm, "endDerivative": vector(-9.98, 3.14) * mm});
            skFitSpline(sketch, "E195", {"points": [v(35.46, -13.21) * mm, v(32.48, -11.64) * mm, v(29.58, -8.33) * mm, v(29.58, -4.39) * mm], "startDerivative": vector(-9.71, 3.25) * mm, "endDerivative": vector(1.84, 11.8) * mm});
            skFitSpline(sketch, "E196", {"points": [v(35.86, -11.8) * mm, v(35.78, -8.44) * mm, v(33.2, -5.7) * mm, v(29.58, -4.39) * mm], "startDerivative": vector(1.32, 10.74) * mm, "endDerivative": vector(-10.86, 2.85) * mm});
            skFitSpline(sketch, "E197", {"points": [v(36.6, -17.23) * mm, v(39.21, -18.04) * mm, v(44.13, -14.67) * mm], "startDerivative": vector(6.13, -3.5) * mm, "endDerivative": vector(8.77, 7.93) * mm});
            skFitSpline(sketch, "E198", {"points": [v(37.2, -14.85) * mm, v(40.01, -13.36) * mm, v(44.13, -14.67) * mm], "startDerivative": vector(5.74, 4.55) * mm, "endDerivative": vector(8.07, -3.97) * mm});
            skFitSpline(sketch, "E199", {"points": [v(37.71, -12.22) * mm, v(40.54, -13.36) * mm, v(45.22, -10.76) * mm, v(46.4, -8.6) * mm], "startDerivative": vector(8.08, -5.84) * mm, "endDerivative": vector(2.51, 7.44) * mm});
            skFitSpline(sketch, "E200", {"points": [v(37.86, -11.2) * mm, v(40.7, -8.35) * mm, v(46.4, -8.6) * mm], "startDerivative": vector(5.27, 7.78) * mm, "endDerivative": vector(11.65, -2.28) * mm});
            skFitSpline(sketch, "E201", {"points": [v(38.08, -7.8) * mm, v(41.47, -8.14) * mm, v(45.12, -4.39) * mm, v(46.4, 0) * mm], "startDerivative": vector(11.52, -3.68) * mm, "endDerivative": vector(2.25, 12.72) * mm});
            skFitSpline(sketch, "E202", {"points": [v(38, -5.7) * mm, v(40.7, -1.7) * mm, v(44.13, 0) * mm, v(46.4, 0) * mm], "startDerivative": vector(6.06, 11.46) * mm, "endDerivative": vector(8.06, -0.85) * mm});
            skFitSpline(sketch, "E203", {"points": [v(37.56, -2.67) * mm, v(41.46, 0) * mm, v(41.94, 7.48) * mm, v(41.54, 8.27) * mm], "startDerivative": vector(12.91, 4.28) * mm, "endDerivative": vector(-2.28, 4.28) * mm});
            skFitSpline(sketch, "E204", {"points": [v(36.8, 0) * mm, v(36.8, 2.92) * mm, v(41.54, 8.27) * mm], "startDerivative": vector(-1.56, 7.68) * mm, "endDerivative": vector(10.24, 9.49) * mm});
            skFitSpline(sketch, "E205", {"points": [v(35.46, 2.92) * mm, v(37.9, 6.34) * mm, v(36.8, 13.46) * mm, v(35.72, 16.36) * mm], "startDerivative": vector(10.36, 9.29) * mm, "endDerivative": vector(-3.55, 9.01) * mm});
            skFitSpline(sketch, "E206", {"points": [v(33.08, 6.13) * mm, v(32.65, 8.37) * mm, v(33.13, 10.98) * mm], "startDerivative": vector(-1.34, 4.57) * mm, "endDerivative": vector(1.4, 5.12) * mm});
            skFitSpline(sketch, "E207", {"points": [v(31.45, 8.27) * mm, v(31.92, 10.98) * mm, v(31.45, 13.87) * mm, v(25.57, 17.53) * mm], "startDerivative": vector(3.31, 8.34) * mm, "endDerivative": vector(-15.07, 7.35) * mm});
            skFitSpline(sketch, "E208", {"points": [v(31.31, 8.14) * mm, v(27.48, 9.67) * mm, v(25.46, 14.84) * mm, v(25.57, 17.53) * mm], "startDerivative": vector(-12.33, 2.05) * mm, "endDerivative": vector(2.61, 8.08) * mm});
            skFitSpline(sketch, "E209", {"points": [v(35.6, 0) * mm, v(31.31, 0) * mm, v(26.67, 2.47) * mm, v(24.97, 4.58) * mm], "startDerivative": vector(-12.16, -1.58) * mm, "endDerivative": vector(-4.88, 7.6) * mm});
            skFitSpline(sketch, "E210", {"points": [v(34.42, 2.92) * mm, v(31.31, 5.3) * mm, v(25.57, 5.62) * mm, v(24.97, 4.58) * mm], "startDerivative": vector(-6.52, 7.01) * mm, "endDerivative": vector(-2.33, -5.58) * mm});
            skFitSpline(sketch, "E211", {"points": [v(37.2, -6.1) * mm, v(33.2, -5.7) * mm, v(30.82, -3.35) * mm, v(29.01, 0) * mm, v(31.31, 0) * mm, v(34.2, -0.18) * mm, v(36.55, -2.37) * mm], "startDerivative": vector(-22.8, -0.84) * mm, "endDerivative": vector(12.26, -17.77) * mm});
            skFitSpline(sketch, "E212", {"points": [v(32.57, -26.74) * mm, v(34.95, -26.8) * mm, v(38.7, -24.2) * mm], "startDerivative": vector(5.5, -1.08) * mm, "endDerivative": vector(6.68, 5.8) * mm});
            skFitSpline(sketch, "E213", {"points": [v(34.8, -22.47) * mm, v(36.82, -22.85) * mm, v(38.7, -24.2) * mm], "startDerivative": vector(4.28, -0.35) * mm, "endDerivative": vector(3.51, -3.08) * mm});
            skFitSpline(sketch, "E214", {"points": [v(35.08, -21.92) * mm, v(36.82, -22.85) * mm, v(40.19, -21.9) * mm, v(42.1, -20.07) * mm], "startDerivative": vector(5.3, -4.44) * mm, "endDerivative": vector(4.84, 5.85) * mm});
            skFitSpline(sketch, "E215", {"points": [v(36.22, -18.56) * mm, v(38.7, -18.06) * mm, v(42.1, -20.07) * mm], "startDerivative": vector(5.46, 2.14) * mm, "endDerivative": vector(6.3, -4.9) * mm});
            skLineSegment(sketch, "E216", {"start": v(31.85, -13.63) * mm, "end": v(31.85, -13.98) * mm});
            skLineSegment(sketch, "E217", {"start": v(31.85, -13.98) * mm, "end": v(34.34, -16.05) * mm});
            skLineSegment(sketch, "E218", {"start": v(31.85, -13.63) * mm, "end": v(34.42, -14.9) * mm});
            skLineSegment(sketch, "E219", {"start": v(36.7, -12.67) * mm, "end": v(34.42, -10.32) * mm});
            skLineSegment(sketch, "E220", {"start": v(34.42, -10.32) * mm, "end": v(34.02, -10.24) * mm});
            skLineSegment(sketch, "E221", {"start": v(34.02, -10.24) * mm, "end": v(36.22, -14.08) * mm});
            skLineSegment(sketch, "E222", {"start": v(37.71, -12.22) * mm, "end": v(40.9, -11.37) * mm});
            skLineSegment(sketch, "E223", {"start": v(40.9, -11.37) * mm, "end": v(40.32, -11.09) * mm});
            skLineSegment(sketch, "E224", {"start": v(40.32, -11.09) * mm, "end": v(37.71, -11.79) * mm});
            skLineSegment(sketch, "E225", {"start": v(36.73, -16.75) * mm, "end": v(40.4, -16.26) * mm});
            skLineSegment(sketch, "E226", {"start": v(40.4, -16.26) * mm, "end": v(39.8, -15.9) * mm});
            skLineSegment(sketch, "E227", {"start": v(39.8, -15.9) * mm, "end": v(36.95, -15.9) * mm});
            skLineSegment(sketch, "E228", {"start": v(35.34, -21.23) * mm, "end": v(39.05, -20.67) * mm});
            skLineSegment(sketch, "E229", {"start": v(39.05, -20.67) * mm, "end": v(38.55, -20.42) * mm});
            skLineSegment(sketch, "E230", {"start": v(38.55, -20.42) * mm, "end": v(35.62, -20.42) * mm});
            skLineSegment(sketch, "E231", {"start": v(38.5, -7.94) * mm, "end": v(42.06, -4.54) * mm});
            skLineSegment(sketch, "E232", {"start": v(42.06, -4.54) * mm, "end": v(41.2, -4.62) * mm});
            skLineSegment(sketch, "E233", {"start": v(41.2, -4.62) * mm, "end": v(38.08, -7.35) * mm});
            skLineSegment(sketch, "E234", {"start": v(37.2, -6.1) * mm, "end": v(33.83, -3.06) * mm});
            skLineSegment(sketch, "E235", {"start": v(33.83, -3.06) * mm, "end": v(34.44, -3.06) * mm});
            skLineSegment(sketch, "E236", {"start": v(34.44, -3.06) * mm, "end": v(37.08, -5.3) * mm});
            skLineSegment(sketch, "E237", {"start": v(37.95, -2.54) * mm, "end": v(39.7, 2.27) * mm});
            skLineSegment(sketch, "E238", {"start": v(39.7, 2.27) * mm, "end": v(39.22, 1.97) * mm});
            skLineSegment(sketch, "E239", {"start": v(39.22, 1.97) * mm, "end": v(37.4, -1.97) * mm});
            skLineSegment(sketch, "E240", {"start": v(35.2, 0.98) * mm, "end": v(31.42, 2.68) * mm});
            skLineSegment(sketch, "E241", {"start": v(31.42, 2.68) * mm, "end": v(31.5, 2.27) * mm});
            skLineSegment(sketch, "E242", {"start": v(31.5, 2.27) * mm, "end": v(35.6, 0) * mm});
            skLineSegment(sketch, "E243", {"start": v(35.8, 3.21) * mm, "end": v(35.46, 9.46) * mm});
            skLineSegment(sketch, "E244", {"start": v(35.46, 9.46) * mm, "end": v(35.04, 9) * mm});
            skLineSegment(sketch, "E245", {"start": v(35.04, 9) * mm, "end": v(34.75, 3.79) * mm});
            skLineSegment(sketch, "E246", {"start": v(-17.05, -33.37) * mm, "end": v(-16.8, -28.36) * mm});
            skLineSegment(sketch, "E247", {"start": v(-16.8, -28.36) * mm, "end": v(-14.87, -32.57) * mm});
            skLineSegment(sketch, "E248", {"start": v(-14.87, -32.57) * mm, "end": v(-17.05, -33.37) * mm});
            skLineSegment(sketch, "E249", {"start": v(-17.64, -36.97) * mm, "end": v(-17.64, -34.67) * mm});
            skLineSegment(sketch, "E250", {"start": v(-17.64, -34.67) * mm, "end": v(-14.22, -33.78) * mm});
            skLineSegment(sketch, "E251", {"start": v(-14.22, -33.78) * mm, "end": v(-12.86, -36.6) * mm});
            skFitSpline(sketch, "E252", {"points": [v(-12.86, -36.6) * mm, v(-10.84, -35.64) * mm, v(-7.27, -35.32) * mm], "startDerivative": vector(4.19, 2.5) * mm, "endDerivative": vector(6.89, 0.14) * mm});
            skFitSpline(sketch, "E253", {"points": [v(-7.84, -25.54) * mm, v(-5.98, -25.62) * mm, v(-5.66, -27.8) * mm, v(-6.47, -28.85) * mm, v(-7.68, -28.93) * mm], "startDerivative": vector(8.15, 1.7) * mm, "endDerivative": vector(-5.95, 0.45) * mm});
            skFitSpline(sketch, "E254", {"points": [v(-6.38, -24.17) * mm, v(-3.88, -24.33) * mm, v(-2.34, -26.35) * mm, v(-2.59, -28.61) * mm, v(-3.88, -29.1) * mm], "startDerivative": vector(9.86, 1) * mm, "endDerivative": vector(-7.4, -0.93) * mm});
            skFitSpline(sketch, "E255", {"points": [v(-3.94, -29.86) * mm, v(-2.97, -29.94) * mm, v(-2.12, -31.76) * mm, v(-1.98, -33.44) * mm, v(-1.84, -33.98) * mm, v(-1.4, -34.63) * mm], "startDerivative": vector(5.53, 0.93) * mm, "endDerivative": vector(3.08, -4.05) * mm});
            skLineSegment(sketch, "E256", {"start": v(-6.38, -24.17) * mm, "end": v(-11.25, -24.5) * mm});
            skLineSegment(sketch, "E257", {"start": v(-11.25, -24.5) * mm, "end": v(-10.84, -33.62) * mm});
            skLineSegment(sketch, "E258", {"start": v(-7.27, -35.32) * mm, "end": v(-7.55, -30.2) * mm});
            skLineSegment(sketch, "E259", {"start": v(-7.84, -25.54) * mm, "end": v(-7.68, -28.93) * mm});
            skLineSegment(sketch, "E260", {"start": v(-5.04, -35.2) * mm, "end": v(-0.38, -35.2) * mm});
            skLineSegment(sketch, "E261", {"start": v(-0.38, -35.2) * mm, "end": v(0, -28) * mm});
            skLineSegment(sketch, "E262", {"start": v(0, -28) * mm, "end": v(1.66, -35.14) * mm});
            skLineSegment(sketch, "E263", {"start": v(1.66, -35.14) * mm, "end": v(3.73, -35.14) * mm});
            skLineSegment(sketch, "E264", {"start": v(3.73, -35.14) * mm, "end": v(6.14, -27.93) * mm});
            skLineSegment(sketch, "E265", {"start": v(6.14, -27.93) * mm, "end": v(5.67, -35.27) * mm});
            skLineSegment(sketch, "E266", {"start": v(5.67, -35.27) * mm, "end": v(8.75, -35.47) * mm});
            skFitSpline(sketch, "E267", {"points": [v(-7.55, -30.2) * mm, v(-6.46, -30.2) * mm, v(-5.51, -30.96) * mm, v(-5.04, -35.2) * mm], "startDerivative": vector(4.46, 0.47) * mm, "endDerivative": vector(0.12, -10.38) * mm});
            skLineSegment(sketch, "E268", {"start": v(-3.88, -29.1) * mm, "end": v(-3.94, -29.86) * mm});
            skLineSegment(sketch, "E269", {"start": v(-1.4, -34.63) * mm, "end": v(-1.06, -23.72) * mm});
            skLineSegment(sketch, "E270", {"start": v(-1.06, -23.72) * mm, "end": v(2.23, -23.82) * mm});
            skLineSegment(sketch, "E271", {"start": v(2.23, -23.82) * mm, "end": v(3.9, -30.28) * mm});
            skLineSegment(sketch, "E272", {"start": v(3.9, -30.28) * mm, "end": v(6.06, -24.07) * mm});
            skLineSegment(sketch, "E273", {"start": v(6.06, -24.07) * mm, "end": v(9.4, -24.07) * mm});
            skLineSegment(sketch, "E274", {"start": v(9.4, -24.07) * mm, "end": v(9.4, -32.12) * mm});
            skLineSegment(sketch, "E275", {"start": v(9.4, -32.12) * mm, "end": v(9.4, -35.53) * mm});
            skLineSegment(sketch, "E276", {"start": v(9.4, -35.53) * mm, "end": v(8.75, -35.47) * mm});
            skLineSegment(sketch, "E277", {"start": v(10.87, -36.16) * mm, "end": v(14.8, -36.47) * mm});
            skLineSegment(sketch, "E278", {"start": v(14.8, -36.47) * mm, "end": v(15.13, -32.39) * mm});
            skLineSegment(sketch, "E279", {"start": v(15.13, -32.39) * mm, "end": v(16.56, -30.58) * mm});
            skLineSegment(sketch, "E280", {"start": v(16.56, -30.58) * mm, "end": v(19.45, -26.35) * mm});
            skLineSegment(sketch, "E281", {"start": v(19.45, -26.35) * mm, "end": v(17.53, -25.85) * mm});
            skLineSegment(sketch, "E282", {"start": v(17.53, -25.85) * mm, "end": v(14.75, -30.58) * mm});
            skLineSegment(sketch, "E283", {"start": v(14.75, -30.58) * mm, "end": v(13.94, -24.96) * mm});
            skLineSegment(sketch, "E284", {"start": v(13.94, -24.96) * mm, "end": v(10.12, -24.5) * mm});
            skLineSegment(sketch, "E285", {"start": v(10.12, -24.5) * mm, "end": v(11.78, -31.38) * mm});
            skLineSegment(sketch, "E286", {"start": v(11.78, -31.38) * mm, "end": v(10.87, -36.16) * mm});
            skFitSpline(sketch, "E287", {"points": [v(-9.38, -18.6) * mm, v(-10.66, -17.86) * mm, v(-11.53, -16.96) * mm], "startDerivative": vector(-2.63, 1.39) * mm, "endDerivative": vector(-1.67, 2) * mm});
            skFitSpline(sketch, "E288", {"points": [v(-11.53, -16.96) * mm, v(-14.48, -16.96) * mm, v(-18.03, -15.33) * mm], "startDerivative": vector(-6.27, -0.7) * mm, "endDerivative": vector(-6.71, 3.85) * mm});
            skLineSegment(sketch, "E289", {"start": v(-18.03, -15.33) * mm, "end": v(-18.03, -2.27) * mm});
            skLineSegment(sketch, "E290", {"start": v(-18.03, -2.27) * mm, "end": v(-15, 0.86) * mm});
            skLineSegment(sketch, "E291", {"start": v(-15, 0.86) * mm, "end": v(-15, 7.88) * mm});
            skLineSegment(sketch, "E292", {"start": v(-15, 7.88) * mm, "end": v(-15, 12.71) * mm});
            skLineSegment(sketch, "E293", {"start": v(-15, 12.71) * mm, "end": v(-16, 18.04) * mm});
            skLineSegment(sketch, "E294", {"start": v(-16, 18.04) * mm, "end": v(-16.82, 21.22) * mm});
            skLineSegment(sketch, "E295", {"start": v(-16.82, 21.22) * mm, "end": v(-12.37, 23.31) * mm});
            skFitSpline(sketch, "E296", {"points": [v(-12.37, 23.31) * mm, v(-10.9, 23.6) * mm, v(-9.74, 22.83) * mm], "startDerivative": vector(3.04, 1.1) * mm, "endDerivative": vector(2.21, -2.1) * mm});
            skLineSegment(sketch, "E297", {"start": v(-9.74, 22.83) * mm, "end": v(-9.74, 18.85) * mm});
            skFitSpline(sketch, "E298", {"points": [v(-9.74, 18.85) * mm, v(-8.43, 17.86) * mm, v(-2.48, 16.53) * mm, v(1.04, 16.69) * mm, v(5.46, 17.4) * mm, v(8.64, 18.85) * mm], "startDerivative": vector(6.96, -7.51) * mm, "endDerivative": vector(15.08, 8.47) * mm});
            skFitSpline(sketch, "E299", {"points": [v(8.66, 21.77) * mm, v(8.66, 22.7) * mm, v(9.25, 23.05) * mm, v(10.12, 23.5) * mm, v(15.58, 21.45) * mm], "startDerivative": vector(-1.06, 5.92) * mm, "endDerivative": vector(14.4, -6.99) * mm});
            skLineSegment(sketch, "E300", {"start": v(8.66, 21.77) * mm, "end": v(8.64, 18.85) * mm});
            skLineSegment(sketch, "E301", {"start": v(15.58, 21.45) * mm, "end": v(14.88, 16.45) * mm});
            skLineSegment(sketch, "E302", {"start": v(14.88, 16.45) * mm, "end": v(14.26, 12.53) * mm});
            skLineSegment(sketch, "E303", {"start": v(14.26, 12.53) * mm, "end": v(14.26, 1.2) * mm});
            skLineSegment(sketch, "E304", {"start": v(14.26, 1.2) * mm, "end": v(16.99, -2.27) * mm});
            skLineSegment(sketch, "E305", {"start": v(16.99, -2.27) * mm, "end": v(17.14, -10.43) * mm});
            skLineSegment(sketch, "E306", {"start": v(17.14, -10.43) * mm, "end": v(17.24, -15.33) * mm});
            skFitSpline(sketch, "E307", {"points": [v(17.24, -15.33) * mm, v(13.83, -16.68) * mm, v(10.69, -17.04) * mm, v(8.32, -18.96) * mm], "startDerivative": vector(-9.54, -4.92) * mm, "endDerivative": vector(-6.8, -7.47) * mm});
            skFitSpline(sketch, "E308", {"points": [v(5.85, -10.5) * mm, v(6.53, -11.78) * mm, v(8.11, -12.39) * mm, v(9.81, -11.9) * mm, v(10.5, -10.46) * mm], "startDerivative": vector(3.02, -5.5) * mm, "endDerivative": vector(1.68, 4.38) * mm});
            skFitSpline(sketch, "E309", {"points": [v(11.25, -10.46) * mm, v(11.89, -11.82) * mm, v(13.29, -12.5) * mm, v(15.29, -11.78) * mm, v(15.93, -10.46) * mm], "startDerivative": vector(2.07, -4.05) * mm, "endDerivative": vector(2.78, 3.3) * mm});
            skLineSegment(sketch, "E310", {"start": v(5.85, -10.5) * mm, "end": v(5.85, -3.14) * mm});
            skLineSegment(sketch, "E311", {"start": v(5.85, -3.14) * mm, "end": v(10.72, -3.14) * mm});
            skLineSegment(sketch, "E312", {"start": v(10.5, -10.46) * mm, "end": v(10.72, -3.14) * mm});
            skLineSegment(sketch, "E313", {"start": v(15.93, -10.46) * mm, "end": v(15.93, -6.91) * mm});
            skLineSegment(sketch, "E314", {"start": v(15.93, -6.91) * mm, "end": v(15.93, -3.14) * mm});
            skLineSegment(sketch, "E315", {"start": v(15.93, -3.14) * mm, "end": v(11.32, -3.14) * mm});
            skLineSegment(sketch, "E316", {"start": v(11.32, -3.14) * mm, "end": v(11.25, -10.46) * mm});
            skLineSegment(sketch, "E317", {"start": v(6.41, -3.82) * mm, "end": v(9.93, -3.82) * mm});
            skLineSegment(sketch, "E318", {"start": v(9.93, -3.82) * mm, "end": v(9.93, -10.46) * mm});
            skLineSegment(sketch, "E319", {"start": v(6.41, -3.82) * mm, "end": v(6.41, -10.35) * mm});
            skLineSegment(sketch, "E320", {"start": v(11.96, -3.85) * mm, "end": v(15.17, -3.89) * mm});
            skLineSegment(sketch, "E321", {"start": v(15.17, -3.89) * mm, "end": v(15.17, -10.16) * mm});
            skLineSegment(sketch, "E322", {"start": v(11.96, -3.85) * mm, "end": v(11.96, -10.42) * mm});
            skFitSpline(sketch, "E323", {"points": [v(6.41, -10.35) * mm, v(7.06, -11.37) * mm, v(8.26, -11.78) * mm, v(9.55, -11.4) * mm, v(9.93, -10.46) * mm], "startDerivative": vector(2.08, -4.57) * mm, "endDerivative": vector(0.86, 4.62) * mm});
            skFitSpline(sketch, "E324", {"points": [v(11.96, -10.42) * mm, v(12.46, -11.37) * mm, v(13.4, -11.78) * mm, v(14.83, -11.25) * mm, v(15.17, -10.16) * mm], "startDerivative": vector(1.67, -4.38) * mm, "endDerivative": vector(0.42, 4.88) * mm});
            skLineSegment(sketch, "E325", {"start": v(-8.21, -7.87) * mm, "end": v(-8.21, -10.83) * mm});
            skLineSegment(sketch, "E326", {"start": v(-8.21, -10.83) * mm, "end": v(-6.68, -10.83) * mm});
            skLineSegment(sketch, "E327", {"start": v(-6.68, -10.83) * mm, "end": v(-6.68, -7.82) * mm});
            skLineSegment(sketch, "E328", {"start": v(-6.68, -7.82) * mm, "end": v(-8.21, -7.87) * mm});
            skLineSegment(sketch, "E329", {"start": v(-8.84, -11.73) * mm, "end": v(-5.7, -11.73) * mm});
            skLineSegment(sketch, "E330", {"start": v(-5.7, -11.73) * mm, "end": v(-5.7, -7.24) * mm});
            skLineSegment(sketch, "E331", {"start": v(-5.7, -7.24) * mm, "end": v(-8.97, -7.24) * mm});
            skLineSegment(sketch, "E332", {"start": v(-8.97, -7.24) * mm, "end": v(-8.84, -11.73) * mm});
            skLineSegment(sketch, "E333", {"start": v(-4.89, -11.23) * mm, "end": v(-4.84, -10.34) * mm});
            skLineSegment(sketch, "E334", {"start": v(-4.84, -10.34) * mm, "end": v(-4.87, -7.87) * mm});
            skPoint(sketch, "E334.endSnap0", {"position": v(-4.87, -10.79) * mm});
            skLineSegment(sketch, "E335", {"start": v(-4.87, -7.87) * mm, "end": v(-3, -7.96) * mm});
            skLineSegment(sketch, "E336", {"start": v(-3, -7.96) * mm, "end": v(-3, -11.23) * mm});
            skLineSegment(sketch, "E337", {"start": v(-3, -11.23) * mm, "end": v(-4.89, -11.23) * mm});
            skLineSegment(sketch, "E338", {"start": v(-2.28, -7.2) * mm, "end": v(-2.28, -12.09) * mm});
            skLineSegment(sketch, "E339", {"start": v(-2.28, -12.09) * mm, "end": v(-5.3, -11.94) * mm});
            skLineSegment(sketch, "E340", {"start": v(-5.3, -11.94) * mm, "end": v(-5.3, -7.15) * mm});
            skLineSegment(sketch, "E341", {"start": v(-5.3, -7.15) * mm, "end": v(-2.28, -7.2) * mm});
            skLineSegment(sketch, "E342", {"start": v(-16.87, -7.47) * mm, "end": v(-16.26, -7.47) * mm});
            skLineSegment(sketch, "E343", {"start": v(-16.26, -7.47) * mm, "end": v(-16.26, -5.12) * mm});
            skLineSegment(sketch, "E344", {"start": v(-16.26, -5.12) * mm, "end": v(-16.64, -5.12) * mm});
            skLineSegment(sketch, "E345", {"start": v(-16.64, -5.12) * mm, "end": v(-16.64, -3.66) * mm});
            skLineSegment(sketch, "E346", {"start": v(-16.64, -3.66) * mm, "end": v(-15.4, -3.66) * mm});
            skLineSegment(sketch, "E347", {"start": v(-15.4, -3.66) * mm, "end": v(-15.44, -3.41) * mm});
            skLineSegment(sketch, "E348", {"start": v(-15.44, -3.41) * mm, "end": v(-15.79, -3.28) * mm});
            skLineSegment(sketch, "E349", {"start": v(-15.79, -3.28) * mm, "end": v(-15.79, -2.36) * mm});
            skLineSegment(sketch, "E350", {"start": v(-15.79, -2.36) * mm, "end": v(-15.34, -2.08) * mm});
            skLineSegment(sketch, "E351", {"start": v(-15.34, -2.08) * mm, "end": v(-11.7, -2.01) * mm});
            skLineSegment(sketch, "E352", {"start": v(-11.7, -2.01) * mm, "end": v(-11, -2.9) * mm});
            skLineSegment(sketch, "E353", {"start": v(-11, -2.9) * mm, "end": v(-9.72, -2.9) * mm});
            skLineSegment(sketch, "E354", {"start": v(-9.72, -2.9) * mm, "end": v(-9, -4.08) * mm});
            skLineSegment(sketch, "E355", {"start": v(-9, -4.08) * mm, "end": v(-9, -5.57) * mm});
            skLineSegment(sketch, "E356", {"start": v(-9, -5.57) * mm, "end": v(-9.75, -5.5) * mm});
            skLineSegment(sketch, "E357", {"start": v(-9.75, -5.5) * mm, "end": v(-9.75, -4.14) * mm});
            skLineSegment(sketch, "E358", {"start": v(-9.75, -4.14) * mm, "end": v(-10.07, -3.66) * mm});
            skLineSegment(sketch, "E359", {"start": v(-10.07, -3.66) * mm, "end": v(-11.02, -3.57) * mm});
            skLineSegment(sketch, "E360", {"start": v(-11.02, -3.57) * mm, "end": v(-11.91, -2.52) * mm});
            skLineSegment(sketch, "E361", {"start": v(-11.91, -2.52) * mm, "end": v(-12.8, -2.52) * mm});
            skLineSegment(sketch, "E362", {"start": v(-12.8, -2.52) * mm, "end": v(-12.8, -3.1) * mm});
            skLineSegment(sketch, "E363", {"start": v(-12.8, -3.1) * mm, "end": v(-12.33, -3.1) * mm});
            skLineSegment(sketch, "E364", {"start": v(-12.33, -3.1) * mm, "end": v(-11.98, -3.8) * mm});
            skLineSegment(sketch, "E365", {"start": v(-11.98, -3.8) * mm, "end": v(-11, -3.8) * mm});
            skLineSegment(sketch, "E366", {"start": v(-11, -3.8) * mm, "end": v(-10.36, -4.24) * mm});
            skLineSegment(sketch, "E367", {"start": v(-10.36, -4.24) * mm, "end": v(-10.36, -5.41) * mm});
            skLineSegment(sketch, "E368", {"start": v(-10.36, -5.41) * mm, "end": v(-10.68, -5.38) * mm});
            skLineSegment(sketch, "E369", {"start": v(-10.68, -5.38) * mm, "end": v(-10.68, -7.35) * mm});
            skLineSegment(sketch, "E370", {"start": v(-10.68, -7.35) * mm, "end": v(-9.86, -7.43) * mm});
            skLineSegment(sketch, "E371", {"start": v(-9.86, -7.43) * mm, "end": v(-9.86, -11.25) * mm});
            skLineSegment(sketch, "E372", {"start": v(-9.86, -11.25) * mm, "end": v(-10.36, -11.67) * mm});
            skLineSegment(sketch, "E373", {"start": v(-10.36, -11.67) * mm, "end": v(-10.74, -11.63) * mm});
            skLineSegment(sketch, "E374", {"start": v(-10.74, -11.63) * mm, "end": v(-10.74, -13.1) * mm});
            skLineSegment(sketch, "E375", {"start": v(-10.74, -13.1) * mm, "end": v(-10.36, -13.13) * mm});
            skLineSegment(sketch, "E376", {"start": v(-10.36, -13.13) * mm, "end": v(-10.36, -15.23) * mm});
            skLineSegment(sketch, "E377", {"start": v(-10.36, -15.23) * mm, "end": v(-16.7, -15.23) * mm});
            skLineSegment(sketch, "E378", {"start": v(-16.7, -15.23) * mm, "end": v(-16.7, -13.19) * mm});
            skLineSegment(sketch, "E379", {"start": v(-16.7, -13.19) * mm, "end": v(-16.24, -13.24) * mm});
            skLineSegment(sketch, "E380", {"start": v(-16.24, -13.24) * mm, "end": v(-16.23, -11.82) * mm});
            skLineSegment(sketch, "E381", {"start": v(-16.23, -11.82) * mm, "end": v(-16.93, -11.82) * mm});
            skLineSegment(sketch, "E382", {"start": v(-16.93, -11.82) * mm, "end": v(-16.87, -7.47) * mm});
            skLineSegment(sketch, "E383", {"start": v(-15.57, -5.12) * mm, "end": v(-15.57, -7.47) * mm});
            skLineSegment(sketch, "E384", {"start": v(-15.57, -7.47) * mm, "end": v(-11.12, -7.47) * mm});
            skLineSegment(sketch, "E385", {"start": v(-11.12, -7.47) * mm, "end": v(-11.12, -5.03) * mm});
            skLineSegment(sketch, "E386", {"start": v(-11.12, -5.03) * mm, "end": v(-15.57, -5.12) * mm});
            skLineSegment(sketch, "E387", {"start": v(-16.26, -10.8) * mm, "end": v(-16.26, -8.08) * mm});
            skLineSegment(sketch, "E388", {"start": v(-16.26, -8.08) * mm, "end": v(-10.36, -8.16) * mm});
            skLineSegment(sketch, "E389", {"start": v(-10.36, -8.16) * mm, "end": v(-10.36, -10.71) * mm});
            skLineSegment(sketch, "E390", {"start": v(-10.36, -10.71) * mm, "end": v(-16.26, -10.8) * mm});
            skLineSegment(sketch, "E391", {"start": v(-15.66, -13.25) * mm, "end": v(-15.66, -11.6) * mm});
            skLineSegment(sketch, "E392", {"start": v(-15.66, -11.6) * mm, "end": v(-11.18, -11.6) * mm});
            skLineSegment(sketch, "E393", {"start": v(-11.18, -11.6) * mm, "end": v(-11.18, -13.32) * mm});
            skLineSegment(sketch, "E394", {"start": v(-11.18, -13.32) * mm, "end": v(-15.66, -13.25) * mm});
            skLineSegment(sketch, "E395", {"start": v(-16.04, -4.17) * mm, "end": v(-16.04, -4.58) * mm});
            skLineSegment(sketch, "E396", {"start": v(-16.04, -4.58) * mm, "end": v(-10.9, -4.58) * mm});
            skLineSegment(sketch, "E397", {"start": v(-10.9, -4.58) * mm, "end": v(-10.9, -4.08) * mm});
            skLineSegment(sketch, "E398", {"start": v(-10.9, -4.08) * mm, "end": v(-16.04, -4.17) * mm});
            skLineSegment(sketch, "E399", {"start": v(-14.05, -3.3) * mm, "end": v(-14.05, -3.65) * mm});
            skLineSegment(sketch, "E400", {"start": v(-14.05, -3.65) * mm, "end": v(-12.62, -3.8) * mm});
            skLineSegment(sketch, "E401", {"start": v(-12.62, -3.8) * mm, "end": v(-12.64, -3.3) * mm});
            skLineSegment(sketch, "E402", {"start": v(-12.64, -3.3) * mm, "end": v(-14.05, -3.3) * mm});
            skLineSegment(sketch, "E403", {"start": v(-14.93, -3.3) * mm, "end": v(-14.92, -3.8) * mm});
            skLineSegment(sketch, "E404", {"start": v(-14.92, -3.8) * mm, "end": v(-14.42, -3.8) * mm});
            skLineSegment(sketch, "E405", {"start": v(-14.42, -3.8) * mm, "end": v(-14.43, -3.3) * mm});
            skLineSegment(sketch, "E406", {"start": v(-14.43, -3.3) * mm, "end": v(-14.93, -3.3) * mm});
            skLineSegment(sketch, "E407", {"start": v(-2.05, 10.25) * mm, "end": v(-2.05, 2.62) * mm});
            skLineSegment(sketch, "E408", {"start": v(-2.05, 2.62) * mm, "end": v(1.27, 2.62) * mm});
            skLineSegment(sketch, "E409", {"start": v(1.27, 2.62) * mm, "end": v(1.27, 10.25) * mm});
            skLineSegment(sketch, "E410", {"start": v(1.27, 10.25) * mm, "end": v(-2.05, 10.25) * mm});
            skLineSegment(sketch, "E411", {"start": v(-4.52, 12.5) * mm, "end": v(-4.52, 10.61) * mm});
            skLineSegment(sketch, "E412", {"start": v(-4.52, 10.61) * mm, "end": v(3.65, 10.57) * mm});
            skLineSegment(sketch, "E413", {"start": v(3.65, 10.57) * mm, "end": v(3.6, 12.5) * mm});
            skLineSegment(sketch, "E414", {"start": v(3.6, 12.5) * mm, "end": v(-4.52, 12.5) * mm});
            skLineSegment(sketch, "E415", {"start": v(4.24, 4.55) * mm, "end": v(4.24, 2.4) * mm});
            skLineSegment(sketch, "E416", {"start": v(4.24, 2.4) * mm, "end": v(8.46, 2.4) * mm});
            skLineSegment(sketch, "E417", {"start": v(8.46, 2.4) * mm, "end": v(8.46, 4.6) * mm});
            skLineSegment(sketch, "E418", {"start": v(8.46, 4.6) * mm, "end": v(4.24, 4.55) * mm});
            skLineSegment(sketch, "E419", {"start": v(7.86, 10.65) * mm, "end": v(7.86, 12.53) * mm});
            skLineSegment(sketch, "E420", {"start": v(7.86, 12.53) * mm, "end": v(11.79, 12.42) * mm});
            skLineSegment(sketch, "E421", {"start": v(11.79, 12.42) * mm, "end": v(11.79, 10.57) * mm});
            skLineSegment(sketch, "E422", {"start": v(11.79, 10.57) * mm, "end": v(7.86, 10.65) * mm});
            skFitSpline(sketch, "E423", {"points": [v(-6.72, 12.46) * mm, v(-5.85, 12.31) * mm, v(-5.28, 11.7) * mm, v(-5.24, 8.53) * mm, v(-6.07, 8.16) * mm], "startDerivative": vector(4.54, -0.49) * mm, "endDerivative": vector(-4.63, -0.25) * mm});
            skFitSpline(sketch, "E424", {"points": [v(-6.04, 7.48) * mm, v(-5.17, 7.29) * mm, v(-4.8, 4.53) * mm, v(-4.98, 3.32) * mm, v(-5.96, 2.53) * mm, v(-7.17, 2.38) * mm], "startDerivative": vector(6.08, 0.72) * mm, "endDerivative": vector(-5.53, 0.68) * mm});
            skLineSegment(sketch, "E425", {"start": v(-6.07, 8.16) * mm, "end": v(-6.04, 7.48) * mm});
            skLineSegment(sketch, "E426", {"start": v(-6.72, 12.46) * mm, "end": v(-9.77, 12.45) * mm});
            skLineSegment(sketch, "E427", {"start": v(-9.77, 12.45) * mm, "end": v(-9.77, 10.76) * mm});
            skLineSegment(sketch, "E428", {"start": v(-9.77, 10.76) * mm, "end": v(-8.23, 10.77) * mm});
            skLineSegment(sketch, "E429", {"start": v(-8.23, 10.77) * mm, "end": v(-8.22, 8.61) * mm});
            skLineSegment(sketch, "E430", {"start": v(-8.22, 8.61) * mm, "end": v(-9.85, 8.61) * mm});
            skLineSegment(sketch, "E431", {"start": v(-9.85, 8.61) * mm, "end": v(-9.85, 6.68) * mm});
            skLineSegment(sketch, "E432", {"start": v(-9.85, 6.68) * mm, "end": v(-8.23, 6.68) * mm});
            skLineSegment(sketch, "E433", {"start": v(-8.23, 6.68) * mm, "end": v(-8.23, 4.2) * mm});
            skLineSegment(sketch, "E434", {"start": v(-8.23, 4.2) * mm, "end": v(-9.74, 4.23) * mm});
            skLineSegment(sketch, "E435", {"start": v(-9.74, 4.23) * mm, "end": v(-9.77, 2.38) * mm});
            skLineSegment(sketch, "E436", {"start": v(-9.77, 2.38) * mm, "end": v(-7.17, 2.38) * mm});
            skFitSpline(sketch, "E437", {"points": [v(7.1, 12.42) * mm, v(5.14, 12.35) * mm, v(4.42, 11.14) * mm, v(4.38, 7.63) * mm, v(6.54, 6.65) * mm, v(8.73, 6.27) * mm, v(9, 4.46) * mm], "startDerivative": vector(-14.28, 1.33) * mm, "endDerivative": vector(-1, -14.31) * mm});
            skFitSpline(sketch, "E438", {"points": [v(7.14, 9.1) * mm, v(9.82, 8.57) * mm, v(11.82, 7.4) * mm, v(11.5, 2.66) * mm, v(9.76, 2.28) * mm, v(8.92, 2.38) * mm], "startDerivative": vector(12.6, -2.33) * mm, "endDerivative": vector(-4.92, -0.43) * mm});
            skLineSegment(sketch, "E439", {"start": v(7.1, 12.42) * mm, "end": v(7.14, 9.1) * mm});
            skLineSegment(sketch, "E440", {"start": v(9, 4.46) * mm, "end": v(9, 3.9) * mm});
            skLineSegment(sketch, "E441", {"start": v(9, 3.9) * mm, "end": v(8.92, 2.38) * mm});
            skLineSegment(sketch, "E442", {"start": v(20.74, 11.95) * mm, "end": v(23.11, 11.95) * mm});
            skLineSegment(sketch, "E443", {"start": v(23.11, 11.95) * mm, "end": v(21.98, 8.43) * mm});
            skLineSegment(sketch, "E444", {"start": v(21.98, 8.43) * mm, "end": v(24.13, 8.43) * mm});
            skLineSegment(sketch, "E445", {"start": v(24.13, 8.43) * mm, "end": v(20.17, 2.4) * mm});
            skLineSegment(sketch, "E446", {"start": v(20.17, 2.4) * mm, "end": v(19.98, 3.49) * mm});
            skLineSegment(sketch, "E447", {"start": v(19.98, 3.49) * mm, "end": v(21.72, 6.96) * mm});
            skLineSegment(sketch, "E448", {"start": v(21.72, 6.96) * mm, "end": v(19.53, 6.96) * mm});
            skLineSegment(sketch, "E449", {"start": v(19.53, 6.96) * mm, "end": v(20.74, 11.95) * mm});
            skCircle(sketch, "E450", {"center": v(3.04, -2) * mm, "radius": 1.19 * mm});
            skCircle(sketch, "E451", {"center": v(8.12, -1.5) * mm, "radius": 0.73 * mm});
            skCircle(sketch, "E452", {"center": v(13.95, -1.93) * mm, "radius": 0.74 * mm});
            skCircle(sketch, "E453", {"center": v(13.95, -1.93) * mm, "radius": 0.39 * mm});
            skCircle(sketch, "E454", {"center": v(8.12, -1.5) * mm, "radius": 0.35 * mm});
            skCircle(sketch, "E455", {"center": v(3.04, -2) * mm, "radius": 0.4 * mm});
            skLineSegment(sketch, "E456", {"start": v(10.23, 21.22) * mm, "end": v(10.58, 21.95) * mm});
            skLineSegment(sketch, "E457", {"start": v(10.58, 21.95) * mm, "end": v(11.68, 21.95) * mm});
            skLineSegment(sketch, "E458", {"start": v(11.68, 21.95) * mm, "end": v(14.66, 20.68) * mm});
            skLineSegment(sketch, "E459", {"start": v(14.66, 20.68) * mm, "end": v(14.24, 19.68) * mm});
            skLineSegment(sketch, "E460", {"start": v(14.24, 19.68) * mm, "end": v(10.23, 21.22) * mm});
            skLineSegment(sketch, "E461", {"start": v(9.66, 20.65) * mm, "end": v(14.3, 18.9) * mm});
            skLineSegment(sketch, "E462", {"start": v(14.3, 18.9) * mm, "end": v(15.11, 20.9) * mm});
            skLineSegment(sketch, "E463", {"start": v(15.11, 20.9) * mm, "end": v(11.55, 22.34) * mm});
            skLineSegment(sketch, "E464", {"start": v(11.55, 22.34) * mm, "end": v(10.4, 22.4) * mm});
            skLineSegment(sketch, "E465", {"start": v(10.4, 22.4) * mm, "end": v(9.66, 20.65) * mm});
            skLineSegment(sketch, "E466", {"start": v(-15.34, 20.7) * mm, "end": v(-15.34, 19.74) * mm});
            skLineSegment(sketch, "E467", {"start": v(-15.34, 19.74) * mm, "end": v(-14.21, 19.71) * mm});
            skLineSegment(sketch, "E468", {"start": v(-14.21, 19.71) * mm, "end": v(-11.12, 21.18) * mm});
            skLineSegment(sketch, "E469", {"start": v(-11.12, 21.18) * mm, "end": v(-11.62, 22.27) * mm});
            skLineSegment(sketch, "E470", {"start": v(-11.62, 22.27) * mm, "end": v(-15.34, 20.7) * mm});
            skLineSegment(sketch, "E471", {"start": v(-15.47, 19.2) * mm, "end": v(-14.13, 19.2) * mm});
            skLineSegment(sketch, "E472", {"start": v(-14.13, 19.2) * mm, "end": v(-10.48, 21.07) * mm});
            skLineSegment(sketch, "E473", {"start": v(-10.48, 21.07) * mm, "end": v(-11.46, 23.02) * mm});
            skLineSegment(sketch, "E474", {"start": v(-11.46, 23.02) * mm, "end": v(-15.79, 21.2) * mm});
            skLineSegment(sketch, "E475", {"start": v(-15.79, 21.2) * mm, "end": v(-15.47, 19.2) * mm});
            skLineSegment(sketch, "E476", {"start": v(-10.38, 2.38) * mm, "end": v(-13.35, 2.38) * mm});
            skLineSegment(sketch, "E477", {"start": v(-13.35, 2.38) * mm, "end": v(-13.35, 12.5) * mm});
            skLineSegment(sketch, "E478", {"start": v(-13.35, 12.5) * mm, "end": v(-10.38, 12.45) * mm});
            skLineSegment(sketch, "E479", {"start": v(-10.38, 12.45) * mm, "end": v(-10.38, 2.38) * mm});
            skFitSpline(sketch, "E480", {"points": [v(-32.36, -12.37) * mm, v(-30.68, -10.97) * mm], "startDerivative": vector(1.68, 1.4) * mm, "endDerivative": vector(1.68, 1.4) * mm});
            skLineSegment(sketch, "E481", {"start": v(33.77, -14.24) * mm, "end": v(34.46, -12.88) * mm});
            skLineSegment(sketch, "E482", {"start": v(34.42, -14.9) * mm, "end": v(35.1, -16.44) * mm});
            skFitSpline(sketch, "E483", {"points": [v(-32.88, -26) * mm, v(-33.94, -23.9) * mm, v(-34.53, -22.65) * mm, v(-35, -21.58) * mm, v(-35.25, -20.95) * mm], "startDerivative": vector(-3.44, 6.77) * mm, "endDerivative": vector(-1.27, 3.26) * mm});
            skFitSpline(sketch, "E484", {"points": [v(-31.36, -25.36) * mm, v(-32.88, -22.65) * mm, v(-33.97, -20.44) * mm], "startDerivative": vector(-3.01, 5.27) * mm, "endDerivative": vector(-2.2, 4.6) * mm});
            skFitSpline(sketch, "E485", {"points": [v(-35.39, -20.57) * mm, v(-35.78, -19.44) * mm, v(-36.11, -17.76) * mm, v(-36.5, -16.73) * mm], "startDerivative": vector(-1.35, 3.28) * mm, "endDerivative": vector(-1.43, 3.08) * mm});
            skFitSpline(sketch, "E486", {"points": [v(-35.82, -14.1) * mm, v(-35.95, -13.4) * mm], "startDerivative": vector(-0.13, 0.72) * mm, "endDerivative": vector(-0.13, 0.72) * mm});
            skFitSpline(sketch, "E487", {"points": [v(-36.56, -16.48) * mm, v(-36.94, -14.42) * mm, v(-37.19, -12.58) * mm, v(-37.21, -12.3) * mm], "startDerivative": vector(-0.9, 4.54) * mm, "endDerivative": vector(-0.13, 1.3) * mm});
            skFitSpline(sketch, "E488", {"points": [v(-37.26, -11.82) * mm, v(-37.37, -10.41) * mm, v(-37.43, -8.42) * mm], "startDerivative": vector(-0.26, 2.95) * mm, "endDerivative": vector(-0.08, 3.83) * mm});
            skFitSpline(sketch, "E489", {"points": [v(-37.41, -7.44) * mm, v(-37.41, -5.44) * mm, v(-36.82, -3.15) * mm], "startDerivative": vector(-0.27, 4.12) * mm, "endDerivative": vector(1.42, 4.46) * mm});
            skFitSpline(sketch, "E490", {"points": [v(-36.1, -12.48) * mm, v(-36.56, -9.54) * mm, v(-36.38, -5.86) * mm], "startDerivative": vector(-1.3, 6.03) * mm, "endDerivative": vector(0.69, 7.19) * mm});
            skFitSpline(sketch, "E491", {"points": [v(-36.32, -5.31) * mm, v(-35.78, -3.15) * mm, v(-35.26, -1.35) * mm], "startDerivative": vector(1.03, 4.25) * mm, "endDerivative": vector(1.11, 3.67) * mm});
            skFitSpline(sketch, "E492", {"points": [v(-36.52, -2.17) * mm, v(-35.96, -0.73) * mm, v(-34.92, 1.64) * mm, v(-34.09, 2.66) * mm, v(-33.86, 3.18) * mm], "startDerivative": vector(2.02, 4.95) * mm, "endDerivative": vector(0.99, 3.24) * mm});
            skFitSpline(sketch, "E493", {"points": [v(-34.02, 1.27) * mm, v(-33.48, 2.66) * mm, v(-32.61, 3.95) * mm], "startDerivative": vector(0.94, 2.87) * mm, "endDerivative": vector(1.88, 2.5) * mm});
            skFitSpline(sketch, "E494", {"points": [v(-32.61, 3.95) * mm, v(-31.16, 6.88) * mm, v(-28.85, 10.54) * mm], "startDerivative": vector(2.83, 6.16) * mm, "endDerivative": vector(4.64, 6.98) * mm});
            skFitSpline(sketch, "E495", {"points": [v(-33.44, 3.88) * mm, v(-32.88, 4.8) * mm, v(-30.85, 8) * mm, v(-28.85, 10.54) * mm], "startDerivative": vector(2.17, 3.49) * mm, "endDerivative": vector(5.19, 6.21) * mm});
            skFitSpline(sketch, "E496", {"points": [v(29.25, -30.36) * mm, v(32.57, -26.74) * mm, v(35.34, -21.23) * mm], "startDerivative": vector(7.65, 6.93) * mm, "endDerivative": vector(4.72, 11.2) * mm});
            skFitSpline(sketch, "E497", {"points": [v(35.1, -16.44) * mm, v(36.22, -14.08) * mm], "startDerivative": vector(1.11, 2.36) * mm, "endDerivative": vector(1.11, 2.36) * mm});
            skFitSpline(sketch, "E498", {"points": [v(35.62, -20.42) * mm, v(36.22, -18.56) * mm, v(36.73, -16.75) * mm], "startDerivative": vector(1.23, 3.7) * mm, "endDerivative": vector(0.99, 3.64) * mm});
            skFitSpline(sketch, "E499", {"points": [v(36.95, -15.9) * mm, v(37.2, -14.85) * mm, v(37.71, -12.22) * mm], "startDerivative": vector(0.6, 2.38) * mm, "endDerivative": vector(0.9, 4.78) * mm});
            skFitSpline(sketch, "E500", {"points": [v(36.7, -12.67) * mm, v(36.7, -9.8) * mm, v(37.2, -6.1) * mm], "startDerivative": vector(-0.22, 5.96) * mm, "endDerivative": vector(1.2, 7.17) * mm});
            skFitSpline(sketch, "E501", {"points": [v(37.71, -11.79) * mm, v(37.86, -11.2) * mm, v(38.08, -7.8) * mm], "startDerivative": vector(0.53, 1.54) * mm, "endDerivative": vector(0.25, 5.83) * mm});
            skFitSpline(sketch, "E502", {"points": [v(38.08, -7.35) * mm, v(38, -5.7) * mm, v(37.56, -2.67) * mm], "startDerivative": vector(-0.08, 3.6) * mm, "endDerivative": vector(-0.92, 5.65) * mm});
            skFitSpline(sketch, "E503", {"points": [v(37.08, -5.3) * mm, v(36.95, -3.48) * mm, v(36.55, -2.37) * mm, v(35.6, 0) * mm], "startDerivative": vector(0.16, 6.03) * mm, "endDerivative": vector(-1.64, 6.86) * mm});
            skFitSpline(sketch, "E504", {"points": [v(37.4, -1.97) * mm, v(36.8, 0) * mm], "startDerivative": vector(-0.6, 1.97) * mm, "endDerivative": vector(-0.6, 1.97) * mm});
            skFitSpline(sketch, "E505", {"points": [v(36.8, 0) * mm, v(35.46, 2.92) * mm], "startDerivative": vector(-1.56, 2.92) * mm, "endDerivative": vector(-1.56, 2.92) * mm});
            skFitSpline(sketch, "E506", {"points": [v(35.2, 0.98) * mm, v(34.42, 2.92) * mm, v(31.74, 7.24) * mm], "startDerivative": vector(-2.85, 4.26) * mm, "endDerivative": vector(-4, 8.04) * mm});
            skFitSpline(sketch, "E507", {"points": [v(33.08, 6.13) * mm, v(31.45, 8.27) * mm, v(29.51, 11.22) * mm], "startDerivative": vector(-3.46, 4.39) * mm, "endDerivative": vector(-3.66, 5.77) * mm});
            skFitSpline(sketch, "E508", {"points": [v(31.74, 7.24) * mm, v(31.31, 8.14) * mm, v(29.51, 11.22) * mm], "startDerivative": vector(-0.97, 2.23) * mm, "endDerivative": vector(-3.24, 5.4) * mm});
            skFitSpline(sketch, "E509", {"points": [v(34.75, 3.79) * mm, v(33.08, 6.13) * mm], "startDerivative": vector(-1.67, 2.34) * mm, "endDerivative": vector(-1.67, 2.34) * mm});
            skFitSpline(sketch, "E510", {"points": [v(-35.28, -11.6) * mm, v(-35.2, -8.41) * mm, v(-33.3, -6.06) * mm, v(-31.09, -4.76) * mm], "startDerivative": vector(-1.14, 9.56) * mm, "endDerivative": vector(7.1, 3.62) * mm});
            skLineSegment(sketch, "E511", {"start": v(33.14, -16.58) * mm, "end": v(34.34, -16.05) * mm});
            skSolve(sketch);
        }
        {
            var Q0;
            {var subQ1=sQuery(id+"F1.wireOp",EDGE,"E287");Q0=makeQuery(id+"F1.imprint","IMPRINT",FACE,{"disambiguationData":[TD([[makeQuery(id+"F1.imprint","IMPRINT",EDGE,{"derivedFrom":subQ1}),-1.0]])]});}
            var Q1;
            Q1=makeQuery(id+"F1.imprint","IMPRINT",FACE,{"disambiguationData":[TD([[makeQuery(id+"F1.imprint","IMPRINT",EDGE,{"derivedFrom":sQuery(id+"F1.wireOp",EDGE,"E317")}),-1.0]])]});
            var Q2;
            Q2=makeQuery(id+"F1.imprint","IMPRINT",FACE,{"disambiguationData":[TD([[makeQuery(id+"F1.imprint","IMPRINT",EDGE,{"derivedFrom":sQuery(id+"F1.wireOp",EDGE,"E320")}),-1.0]])]});
            var Q3;
            Q3=makeQuery(id+"F1.imprint","IMPRINT",FACE,{"disambiguationData":[TD([[makeQuery(id+"F1.imprint","IMPRINT",EDGE,{"derivedFrom":sQuery(id+"F1.wireOp",EDGE,"E333")}),-1.0]])]});
            var Q4;
            Q4=makeQuery(id+"F1.imprint","IMPRINT",FACE,{"disambiguationData":[TD([[makeQuery(id+"F1.imprint","IMPRINT",EDGE,{"derivedFrom":sQuery(id+"F1.wireOp",EDGE,"E325")}),1.0]])]});
            var Q5;
            Q5=makeQuery(id+"F1.imprint","IMPRINT",FACE,{"disambiguationData":[TD([[makeQuery(id+"F1.imprint","IMPRINT",EDGE,{"derivedFrom":sQuery(id+"F1.wireOp",EDGE,"E442")}),-1.0]])]});
            var Q6;
            Q6=makeQuery(id+"F1.imprint","IMPRINT",FACE,{"disambiguationData":[TD([[makeQuery(id+"F1.imprint","IMPRINT",EDGE,{"derivedFrom":sQuery(id+"F1.wireOp",EDGE,"E131")}),-1.0]])]});
            var Q7;
            Q7=makeQuery(id+"F1.imprint","IMPRINT",FACE,{"disambiguationData":[TD([[makeQuery(id+"F1.imprint","IMPRINT",EDGE,{"derivedFrom":sQuery(id+"F1.wireOp",EDGE,"E50")}),-1.0]])]});
            var Q8;
            {var subQ1=sQuery(id+"F1.wireOp",EDGE,"E161");Q8=makeQuery(id+"F1.imprint","IMPRINT",FACE,{"disambiguationData":[TD([[makeQuery(id+"F1.imprint","IMPRINT",EDGE,{"derivedFrom":subQ1}),1.0]])]});}
            var Q9;
            Q9=makeQuery(id+"F1.imprint","IMPRINT",FACE,{"disambiguationData":[TD([[makeQuery(id+"F1.imprint","IMPRINT",EDGE,{"derivedFrom":sQuery(id+"F1.wireOp",EDGE,"E253")}),-1.0]])]});
            var Q10;
            {var subQ0=sQuery(id+"F1.wireOp",EDGE,"E157");Q10=makeQuery(id+"F1.imprint","IMPRINT",FACE,{"disambiguationData":[TD([[makeQuery(id+"F1.imprint","IMPRINT",EDGE,{"derivedFrom":subQ0}),1.0]])]});}
            var Q11;
            {var subQ0=sQuery(id+"F1.wireOp",EDGE,"E162");Q11=makeQuery(id+"F1.imprint","IMPRINT",FACE,{"disambiguationData":[TD([[makeQuery(id+"F1.imprint","IMPRINT",EDGE,{"derivedFrom":subQ0}),1.0]])]});}
            var Q12;
            {var subQ3=sQuery(id+"F1.wireOp",EDGE,"E180");Q12=makeQuery(id+"F1.imprint","IMPRINT",FACE,{"disambiguationData":[TD([[makeQuery(id+"F1.imprint","IMPRINT",EDGE,{"derivedFrom":subQ3}),1.0]])]});}
            var Q13;
            {var subQ0=sQuery(id+"F1.wireOp",EDGE,"E176");Q13=makeQuery(id+"F1.imprint","IMPRINT",FACE,{"disambiguationData":[TD([[makeQuery(id+"F1.imprint","IMPRINT",EDGE,{"derivedFrom":subQ0}),1.0]])]});}
            extrude(context, id + "F2", {"entities" : qUnion([Q0, Q1, Q2, Q3, Q4, Q5, Q6, Q7, Q8, Q9, Q10, Q11, Q12, Q13]), "depth" : 13.46 * mm});
        }
        {
            var Q0;
            Q0=makeQuery(id+"F1.imprint","IMPRINT",FACE,{"disambiguationData":[TD([[makeQuery(id+"F1.imprint","IMPRINT",EDGE,{"derivedFrom":sQuery(id+"F1.wireOp",EDGE,"E63")}),1.0]])]});
            var Q1;
            Q1=makeQuery(id+"F1.imprint","IMPRINT",FACE,{"disambiguationData":[TD([[makeQuery(id+"F1.imprint","IMPRINT",EDGE,{"derivedFrom":sQuery(id+"F1.wireOp",EDGE,"E184")}),1.0]])]});
            extrude(context, id + "F3", {"entities" : qUnion([Q0, Q1]), "depth" : 12.2 * mm});
        }
        {
            var Q0;
            Q0=makeQuery(id+"F1.imprint","IMPRINT",FACE,{"disambiguationData":[TD([[makeQuery(id+"F1.imprint","IMPRINT",EDGE,{"derivedFrom":sQuery(id+"F1.wireOp",EDGE,"E476")}),-1.0]])]});
            var Q1;
            Q1=makeQuery(id+"F1.imprint","IMPRINT",FACE,{"disambiguationData":[TD([[makeQuery(id+"F1.imprint","IMPRINT",EDGE,{"derivedFrom":sQuery(id+"F1.wireOp",EDGE,"E423")}),-1.0]])]});
            var Q2;
            Q2=makeQuery(id+"F1.imprint","IMPRINT",FACE,{"disambiguationData":[TD([[makeQuery(id+"F1.imprint","IMPRINT",EDGE,{"derivedFrom":sQuery(id+"F1.wireOp",EDGE,"E407")}),1.0]])]});
            var Q3;
            Q3=makeQuery(id+"F1.imprint","IMPRINT",FACE,{"disambiguationData":[TD([[makeQuery(id+"F1.imprint","IMPRINT",EDGE,{"derivedFrom":sQuery(id+"F1.wireOp",EDGE,"E411")}),1.0]])]});
            var Q4;
            Q4=makeQuery(id+"F1.imprint","IMPRINT",FACE,{"disambiguationData":[TD([[makeQuery(id+"F1.imprint","IMPRINT",EDGE,{"derivedFrom":sQuery(id+"F1.wireOp",EDGE,"E437")}),1.0]])]});
            var Q5;
            Q5=makeQuery(id+"F1.imprint","IMPRINT",FACE,{"disambiguationData":[TD([[makeQuery(id+"F1.imprint","IMPRINT",EDGE,{"derivedFrom":sQuery(id+"F1.wireOp",EDGE,"E419")}),-1.0]])]});
            var Q6;
            Q6=makeQuery(id+"F1.imprint","IMPRINT",FACE,{"disambiguationData":[TD([[makeQuery(id+"F1.imprint","IMPRINT",EDGE,{"derivedFrom":sQuery(id+"F1.wireOp",EDGE,"E415")}),1.0]])]});
            var Q7;
            Q7=makeQuery(id+"F1.imprint","IMPRINT",FACE,{"disambiguationData":[TD([[makeQuery(id+"F1.imprint","IMPRINT",EDGE,{"derivedFrom":sQuery(id+"F1.wireOp",EDGE,"E189")}),-1.0]])]});
            var Q8;
            Q8=makeQuery(id+"F1.imprint","IMPRINT",FACE,{"disambiguationData":[TD([[makeQuery(id+"F1.imprint","IMPRINT",EDGE,{"derivedFrom":sQuery(id+"F1.wireOp",EDGE,"E277")}),1.0]])]});
            var Q9;
            Q9=makeQuery(id+"F1.imprint","IMPRINT",FACE,{"disambiguationData":[TD([[makeQuery(id+"F1.imprint","IMPRINT",EDGE,{"derivedFrom":sQuery(id+"F1.wireOp",EDGE,"E131")}),-1.0]])]});
            var Q10;
            Q10=makeQuery(id+"F1.imprint","IMPRINT",FACE,{"disambiguationData":[TD([[makeQuery(id+"F1.imprint","IMPRINT",EDGE,{"derivedFrom":sQuery(id+"F1.wireOp",EDGE,"E442")}),-1.0]])]});
            extrude(context, id + "F4", {"entities" : qUnion([Q0, Q1, Q2, Q3, Q4, Q5, Q6, Q7, Q8, Q9, Q10]), "depth" : 14.73 * mm});
        }
        {
            var Q0;
            {var subQ2=sQuery(id+"F1.wireOp",EDGE,"E174");Q0=makeQuery(id+"F1.imprint","IMPRINT",FACE,{"disambiguationData":[TD([[makeQuery(id+"F1.imprint","IMPRINT",EDGE,{"derivedFrom":subQ2}),-1.0]])]});}
            var Q1;
            {var subQ3=sQuery(id+"F1.wireOp",EDGE,"E75");Q1=makeQuery(id+"F1.imprint","IMPRINT",FACE,{"disambiguationData":[TD([[makeQuery(id+"F1.imprint","IMPRINT",EDGE,{"derivedFrom":subQ3}),1.0]])]});}
            extrude(context, id + "F5", {"entities" : qUnion([Q0, Q1]), "operationType" : NewBodyOperationType.ADD, "depth" : 16.5 * mm});
        }
        {
            var Q0;
            Q0 = qSketchRegion(id + "F0", true);
            extrude(context, id + "F6", {"entities" : qUnion([Q0]), "operationType" : NewBodyOperationType.ADD, "depth" : 15.24 * mm});
        }
        {
            var Q0;
            {var subQ20=sQuery(id+"F1.wireOp",EDGE,"E154");Q0=makeQuery(id+"F1.imprint","IMPRINT",FACE,{"disambiguationData":[TD([[makeQuery(id+"F1.imprint","IMPRINT",EDGE,{"derivedFrom":subQ20}),1.0]])]});}
            var Q1;
            Q1=makeQuery(id+"F1.imprint","IMPRINT",FACE,{"disambiguationData":[TD([[makeQuery(id+"F1.imprint","IMPRINT",EDGE,{"derivedFrom":sQuery(id+"F1.wireOp",EDGE,"E54")}),-1.0]])]});
            extrude(context, id + "F7", {"entities" : qUnion([Q0, Q1]), "depth" : 13.2 * mm});
        }
        {
            var Q0;
            Q0=makeQuery(id+"F1.imprint","IMPRINT",FACE,{"disambiguationData":[TD([[makeQuery(id+"F1.imprint","IMPRINT",EDGE,{"derivedFrom":sQuery(id+"F1.wireOp",EDGE,"E342")}),-1.0]])]});
            var Q1;
            Q1=makeQuery(id+"F1.imprint","IMPRINT",FACE,{"disambiguationData":[TD([[makeQuery(id+"F1.imprint","IMPRINT",EDGE,{"derivedFrom":sQuery(id+"F1.wireOp",EDGE,"E325")}),-1.0]])]});
            var Q2;
            Q2=makeQuery(id+"F1.imprint","IMPRINT",FACE,{"disambiguationData":[TD([[makeQuery(id+"F1.imprint","IMPRINT",EDGE,{"derivedFrom":sQuery(id+"F1.wireOp",EDGE,"E333")}),1.0]])]});
            var Q3;
            Q3=makeQuery(id+"F1.imprint","IMPRINT",FACE,{"disambiguationData":[TD([[makeQuery(id+"F1.imprint","IMPRINT",EDGE,{"derivedFrom":sQuery(id+"F1.wireOp",EDGE,"E308")}),1.0]])]});
            var Q4;
            Q4=makeQuery(id+"F1.imprint","IMPRINT",FACE,{"disambiguationData":[TD([[makeQuery(id+"F1.imprint","IMPRINT",EDGE,{"derivedFrom":sQuery(id+"F1.wireOp",EDGE,"E309")}),1.0]])]});
            var Q5;
            Q5=makeQuery(id+"F1.imprint","IMPRINT",FACE,{"disambiguationData":[TD([[makeQuery(id+"F1.imprint","IMPRINT",EDGE,{"derivedFrom":sQuery(id+"F1.wireOp",EDGE,"E455")}),1.0]])]});
            var Q6;
            Q6=makeQuery(id+"F1.imprint","IMPRINT",FACE,{"disambiguationData":[TD([[makeQuery(id+"F1.imprint","IMPRINT",EDGE,{"derivedFrom":sQuery(id+"F1.wireOp",EDGE,"E453")}),1.0]])]});
            var Q7;
            Q7=makeQuery(id+"F1.imprint","IMPRINT",FACE,{"disambiguationData":[TD([[makeQuery(id+"F1.imprint","IMPRINT",EDGE,{"derivedFrom":sQuery(id+"F1.wireOp",EDGE,"E454")}),1.0]])]});
            extrude(context, id + "F8", {"entities" : qUnion([Q0, Q1, Q2, Q3, Q4, Q5, Q6, Q7]), "depth" : 12.5 * mm});
        }
        {
            var Q0;
            Q0=makeQuery(id+"F1.imprint","IMPRINT",FACE,{"disambiguationData":[TD([[makeQuery(id+"F1.imprint","IMPRINT",EDGE,{"derivedFrom":sQuery(id+"F1.wireOp",EDGE,"E391")}),-1.0]])]});
            var Q1;
            Q1=makeQuery(id+"F1.imprint","IMPRINT",FACE,{"disambiguationData":[TD([[makeQuery(id+"F1.imprint","IMPRINT",EDGE,{"derivedFrom":sQuery(id+"F1.wireOp",EDGE,"E387")}),-1.0]])]});
            var Q2;
            Q2=makeQuery(id+"F1.imprint","IMPRINT",FACE,{"disambiguationData":[TD([[makeQuery(id+"F1.imprint","IMPRINT",EDGE,{"derivedFrom":sQuery(id+"F1.wireOp",EDGE,"E383")}),1.0]])]});
            var Q3;
            Q3=makeQuery(id+"F1.imprint","IMPRINT",FACE,{"disambiguationData":[TD([[makeQuery(id+"F1.imprint","IMPRINT",EDGE,{"derivedFrom":sQuery(id+"F1.wireOp",EDGE,"E395")}),1.0]])]});
            var Q4;
            Q4=makeQuery(id+"F1.imprint","IMPRINT",FACE,{"disambiguationData":[TD([[makeQuery(id+"F1.imprint","IMPRINT",EDGE,{"derivedFrom":sQuery(id+"F1.wireOp",EDGE,"E399")}),1.0]])]});
            var Q5;
            Q5=makeQuery(id+"F1.imprint","IMPRINT",FACE,{"disambiguationData":[TD([[makeQuery(id+"F1.imprint","IMPRINT",EDGE,{"derivedFrom":sQuery(id+"F1.wireOp",EDGE,"E403")}),1.0]])]});
            var Q6;
            Q6=makeQuery(id+"F1.imprint","IMPRINT",FACE,{"disambiguationData":[TD([[makeQuery(id+"F1.imprint","IMPRINT",EDGE,{"derivedFrom":sQuery(id+"F1.wireOp",EDGE,"E450")}),1.0]])]});
            var Q7;
            Q7=makeQuery(id+"F1.imprint","IMPRINT",FACE,{"disambiguationData":[TD([[makeQuery(id+"F1.imprint","IMPRINT",EDGE,{"derivedFrom":sQuery(id+"F1.wireOp",EDGE,"E451")}),1.0]])]});
            var Q8;
            Q8=makeQuery(id+"F1.imprint","IMPRINT",FACE,{"disambiguationData":[TD([[makeQuery(id+"F1.imprint","IMPRINT",EDGE,{"derivedFrom":sQuery(id+"F1.wireOp",EDGE,"E452")}),1.0]])]});
            var Q9;
            Q9=makeQuery(id+"F1.imprint","IMPRINT",FACE,{"disambiguationData":[TD([[makeQuery(id+"F1.imprint","IMPRINT",EDGE,{"derivedFrom":sQuery(id+"F1.wireOp",EDGE,"E246")}),-1.0]])]});
            var Q10;
            Q10=makeQuery(id+"F1.imprint","IMPRINT",FACE,{"disambiguationData":[TD([[makeQuery(id+"F1.imprint","IMPRINT",EDGE,{"derivedFrom":sQuery(id+"F1.wireOp",EDGE,"E253")}),-1.0]])]});
            extrude(context, id + "F9", {"entities" : qUnion([Q0, Q1, Q2, Q3, Q4, Q5, Q6, Q7, Q8, Q9, Q10]), "depth" : 12.2 * mm});
        }
        {
            var Q0;
            Q0=makeQuery(id+"F1.imprint","IMPRINT",FACE,{"disambiguationData":[TD([[makeQuery(id+"F1.imprint","IMPRINT",EDGE,{"derivedFrom":sQuery(id+"F1.wireOp",EDGE,"E456")}),-1.0]])]});
            var Q1;
            Q1=makeQuery(id+"F1.imprint","IMPRINT",FACE,{"disambiguationData":[TD([[makeQuery(id+"F1.imprint","IMPRINT",EDGE,{"derivedFrom":sQuery(id+"F1.wireOp",EDGE,"E466")}),1.0]])]});
            extrude(context, id + "F10", {"entities" : qUnion([Q0, Q1]), "operationType" : NewBodyOperationType.ADD, "depth" : 11.43 * mm});
        }
        {
            var Q0;
            Q0=makeQuery(id+"F1.imprint","IMPRINT",FACE,{"disambiguationData":[TD([[makeQuery(id+"F1.imprint","IMPRINT",EDGE,{"derivedFrom":sQuery(id+"F1.wireOp",EDGE,"E466")}),-1.0]])]});
            extrude(context, id + "F11", {"entities" : qUnion([Q0]), "depth" : 12.06 * mm});
        }
        {
            var Q0;
            Q0=makeQuery(id+"F1.imprint","IMPRINT",FACE,{"disambiguationData":[TD([[makeQuery(id+"F1.imprint","IMPRINT",EDGE,{"derivedFrom":sQuery(id+"F1.wireOp",EDGE,"E456")}),1.0]])]});
            extrude(context, id + "F12", {"entities" : qUnion([Q0]), "depth" : 12.14 * mm});
        }
    });
